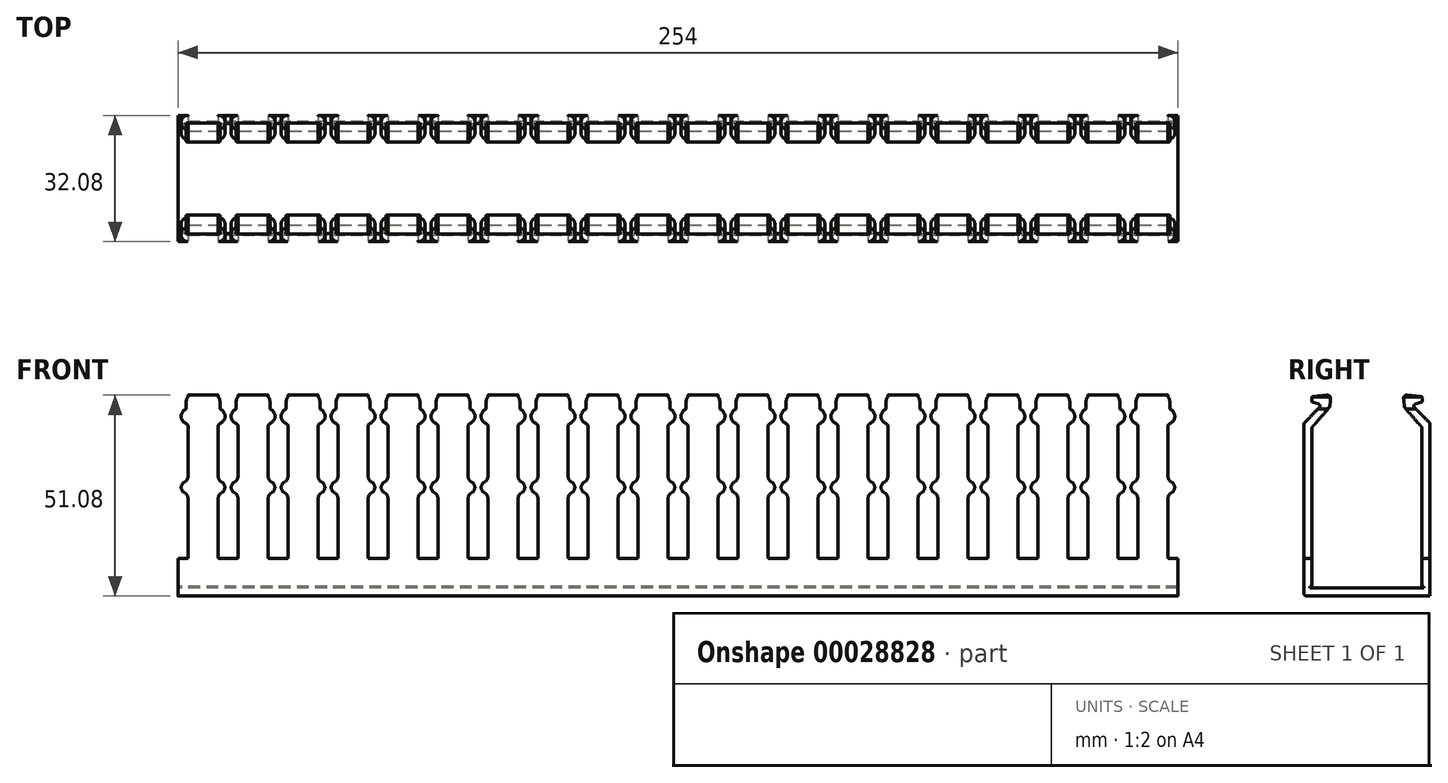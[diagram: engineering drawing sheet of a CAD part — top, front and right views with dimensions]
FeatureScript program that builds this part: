
annotation { "Feature Type Name" : "Feature", "Feature Type Description" : "" }
export const myFeature = defineFeature(function(context is Context, id is Id, definition is map)
    precondition{}
    {
        {
            var Q0;
            Q0=qCreatedBy(makeId("Right.planeOp"),FACE);
            var sketch = newSketch(context, id + "F0", { "sketchPlane" : qUnion([Q0])});
            skLineSegment(sketch, "E0", {"start": v(-14.48, -23.5) * mm, "end": v(-14.48, -23.08) * mm});
            skLineSegment(sketch, "E1", {"start": v(-14.48, -23.08) * mm, "end": v(-14, -23.12) * mm});
            skLineSegment(sketch, "E2", {"start": v(-14, -23.12) * mm, "end": v(-14, 17.02) * mm});
            skArc(sketch, "E3", {"start": v(-14, 17.02) * mm, "mid": v(-13.95, 17.28) * mm, "end": v(-13.81, 17.52) * mm});
            skLineSegment(sketch, "E4", {"start": v(-13.81, 17.52) * mm, "end": v(-9.62, 22.36) * mm});
            skArc(sketch, "E5", {"start": v(-9.62, 22.36) * mm, "mid": v(-9.5, 22.56) * mm, "end": v(-9.44, 22.8) * mm});
            skLineSegment(sketch, "E6", {"start": v(-9.44, 22.8) * mm, "end": v(-9.3, 24.72) * mm});
            skArc(sketch, "E7", {"start": v(-9.3, 24.72) * mm, "mid": v(-9.53, 25.33) * mm, "end": v(-10.13, 25.54) * mm});
            skLineSegment(sketch, "E8", {"start": v(-10.13, 25.54) * mm, "end": v(-13.77, 25.17) * mm});
            skArc(sketch, "E9", {"start": v(-13.77, 25.17) * mm, "mid": v(-13.92, 25.1) * mm, "end": v(-14, 24.94) * mm});
            skLineSegment(sketch, "E10", {"start": v(-14, 24.94) * mm, "end": v(-14.06, 24.06) * mm});
            skArc(sketch, "E11", {"start": v(-14.06, 24.06) * mm, "mid": v(-14.02, 23.9) * mm, "end": v(-13.89, 23.8) * mm});
            skLineSegment(sketch, "E12", {"start": v(-13.89, 23.8) * mm, "end": v(-12.26, 23.23) * mm});
            skArc(sketch, "E13", {"start": v(-12.26, 23.23) * mm, "mid": v(-11.94, 22.87) * mm, "end": v(-12.07, 22.4) * mm});
            skLineSegment(sketch, "E14", {"start": v(-12.07, 22.4) * mm, "end": v(-15.82, 18.57) * mm});
            skArc(sketch, "E15", {"start": v(-15.82, 18.57) * mm, "mid": v(-15.98, 18.32) * mm, "end": v(-16.04, 18.03) * mm});
            skLineSegment(sketch, "E16", {"start": v(-16.04, 18.03) * mm, "end": v(-16.03, -24.78) * mm});
            skArc(sketch, "E17", {"start": v(-16.03, -24.78) * mm, "mid": v(-15.8, -25.32) * mm, "end": v(-15.26, -25.54) * mm});
            skLineSegment(sketch, "E18", {"start": v(-15.26, -25.54) * mm, "end": v(16.03, -25.54) * mm});
            skLineSegment(sketch, "E19", {"start": v(16.03, -25.54) * mm, "end": v(16.04, 18.03) * mm});
            skArc(sketch, "E20", {"start": v(16.04, 18.03) * mm, "mid": v(15.98, 18.32) * mm, "end": v(15.82, 18.57) * mm});
            skLineSegment(sketch, "E21", {"start": v(15.82, 18.57) * mm, "end": v(12.07, 22.4) * mm});
            skArc(sketch, "E22", {"start": v(12.07, 22.4) * mm, "mid": v(11.94, 22.87) * mm, "end": v(12.26, 23.23) * mm});
            skLineSegment(sketch, "E23", {"start": v(12.26, 23.23) * mm, "end": v(13.89, 23.8) * mm});
            skArc(sketch, "E24", {"start": v(13.89, 23.8) * mm, "mid": v(14.02, 23.9) * mm, "end": v(14.06, 24.06) * mm});
            skLineSegment(sketch, "E25", {"start": v(14.06, 24.06) * mm, "end": v(14, 24.94) * mm});
            skArc(sketch, "E26", {"start": v(14, 24.94) * mm, "mid": v(13.92, 25.1) * mm, "end": v(13.77, 25.17) * mm});
            skLineSegment(sketch, "E27", {"start": v(13.77, 25.17) * mm, "end": v(10.13, 25.54) * mm});
            skArc(sketch, "E28", {"start": v(10.13, 25.54) * mm, "mid": v(9.53, 25.33) * mm, "end": v(9.3, 24.72) * mm});
            skLineSegment(sketch, "E29", {"start": v(9.3, 24.72) * mm, "end": v(9.44, 22.8) * mm});
            skArc(sketch, "E30", {"start": v(9.44, 22.8) * mm, "mid": v(9.5, 22.56) * mm, "end": v(9.62, 22.36) * mm});
            skLineSegment(sketch, "E31", {"start": v(9.62, 22.36) * mm, "end": v(13.81, 17.52) * mm});
            skArc(sketch, "E32", {"start": v(13.81, 17.52) * mm, "mid": v(13.95, 17.28) * mm, "end": v(14, 17.02) * mm});
            skLineSegment(sketch, "E33", {"start": v(14, 17.02) * mm, "end": v(14, -23.12) * mm});
            skLineSegment(sketch, "E34", {"start": v(14, -23.12) * mm, "end": v(14.48, -23.08) * mm});
            skLineSegment(sketch, "E35", {"start": v(14.48, -23.08) * mm, "end": v(14.48, -23.5) * mm});
            skLineSegment(sketch, "E36", {"start": v(14.48, -23.5) * mm, "end": v(-14.48, -23.5) * mm});
            skSolve(sketch);
        }
        {
            var Q0;
            Q0=qSketchRegion(id+"F0",true);
            extrude(context, id + "F1", {"entities" : qUnion([Q0]), "endBound" : BoundingType.SYMMETRIC, "depth" : 254 * mm});
        }
        {
            var Q0;
            Q0=qCreatedBy(makeId("Front.planeOp"),FACE);
            var sketch = newSketch(context, id + "F2", { "sketchPlane" : qUnion([Q0])});
            skLineSegment(sketch, "E37.bottom", {"start": v(-2.49, 26.05) * mm, "end": v(2.49, 26.05) * mm});
            skLineSegment(sketch, "E37.top", {"start": v(-2.24, -16.02) * mm, "end": v(2.24, -16.02) * mm});
            skLineSegment(sketch, "E37.right", {"start": v(2.49, 26.05) * mm, "end": v(2.49, 25.07) * mm});
            skPoint(sketch, "E38.visualSharp", {"position": v(2.49, -16.02) * mm});
            skArc(sketch, "E38.filletArc", {"start": v(2.24, -16.02) * mm, "mid": v(2.41, -15.94) * mm, "end": v(2.49, -15.76) * mm});
            skPoint(sketch, "E39.visualSharp", {"position": v(-2.49, -16.02) * mm});
            skArc(sketch, "E39.filletArc", {"start": v(-2.49, -15.76) * mm, "mid": v(-2.41, -15.94) * mm, "end": v(-2.24, -16.02) * mm});
            skArc(sketch, "E40", {"start": v(1.65, 3.46) * mm, "mid": v(0.8, 2.1) * mm, "end": v(1.65, 0.73) * mm});
            skArc(sketch, "E41", {"start": v(1.65, 3.46) * mm, "mid": v(2.26, 4.02) * mm, "end": v(2.49, 4.82) * mm});
            skLineSegment(sketch, "E42", {"start": v(2.33, 2.1) * mm, "end": v(-0.6, 2.1) * mm, "construction": true});
            skArc(sketch, "E43.MirrorC", {"start": v(1.65, 0.73) * mm, "mid": v(2.26, 0.17) * mm, "end": v(2.49, -0.63) * mm});
            skLineSegment(sketch, "E44.trimOffspring", {"start": v(2.49, -0.63) * mm, "end": v(2.49, -15.76) * mm});
            skArc(sketch, "E45.MirrorCS", {"start": v(-1.65, 3.46) * mm, "mid": v(-0.8, 2.1) * mm, "end": v(-1.65, 0.73) * mm});
            skArc(sketch, "E46.MirrorCS", {"start": v(-1.65, 3.46) * mm, "mid": v(-2.26, 4.02) * mm, "end": v(-2.49, 4.82) * mm});
            skArc(sketch, "E47.MirrorCS", {"start": v(-1.65, 0.73) * mm, "mid": v(-2.26, 0.17) * mm, "end": v(-2.49, -0.63) * mm});
            skLineSegment(sketch, "E48.trimOffspring", {"start": v(-2.49, -0.63) * mm, "end": v(-2.49, -15.76) * mm});
            skArc(sketch, "E49", {"start": v(2.08, 22) * mm, "mid": v(0.78, 20.17) * mm, "end": v(2.06, 18.33) * mm});
            skLineSegment(sketch, "E50.trimOffspring", {"start": v(2.49, 17.71) * mm, "end": v(2.49, 4.82) * mm});
            skPoint(sketch, "E51.visualSharp", {"position": v(2.49, 18.23) * mm});
            skArc(sketch, "E51.filletArc", {"start": v(2.49, 17.71) * mm, "mid": v(2.37, 18.09) * mm, "end": v(2.06, 18.33) * mm});
            skLineSegment(sketch, "E52", {"start": v(2.08, 22) * mm, "end": v(2.1, 24.06) * mm});
            skPoint(sketch, "E53.orphan", {"position": v(2.08, 22) * mm});
            skArc(sketch, "E54", {"start": v(2.49, 25.07) * mm, "mid": v(2.2, 24.6) * mm, "end": v(2.1, 24.06) * mm});
            skArc(sketch, "E55.MirrorCS", {"start": v(-2.49, 17.71) * mm, "mid": v(-2.37, 18.09) * mm, "end": v(-2.06, 18.33) * mm});
            skArc(sketch, "E56.MirrorCS", {"start": v(-2.08, 22) * mm, "mid": v(-0.78, 20.17) * mm, "end": v(-2.06, 18.33) * mm});
            skPoint(sketch, "E57.MirrorP", {"position": v(-2.08, 22) * mm});
            skLineSegment(sketch, "E58.MirrorCS", {"start": v(-2.08, 22) * mm, "end": v(-2.1, 24.06) * mm});
            skLineSegment(sketch, "E59.MirrorCS", {"start": v(-2.49, 17.71) * mm, "end": v(-2.49, 4.82) * mm});
            skLineSegment(sketch, "E60.MirrorCS", {"start": v(-2.49, 26.05) * mm, "end": v(-2.49, 25.07) * mm});
            skArc(sketch, "E61.MirrorCS", {"start": v(-2.49, 25.07) * mm, "mid": v(-2.2, 24.6) * mm, "end": v(-2.1, 24.06) * mm});
            skPoint(sketch, "E62.MirrorP", {"position": v(-2.49, 18.23) * mm});
            skPoint(sketch, "E63.1.0.1", {"position": v(14.78, 22) * mm});
            skArc(sketch, "E63.1.0.6", {"start": v(10.21, 25.07) * mm, "mid": v(10.5, 24.6) * mm, "end": v(10.6, 24.06) * mm});
            skLineSegment(sketch, "E63.1.0.7", {"start": v(10.21, 26.05) * mm, "end": v(10.21, 25.07) * mm});
            skLineSegment(sketch, "E63.1.0.9", {"start": v(10.62, 22) * mm, "end": v(10.6, 24.06) * mm});
            skArc(sketch, "E63.1.0.11", {"start": v(15.19, 25.07) * mm, "mid": v(14.9, 24.6) * mm, "end": v(14.8, 24.06) * mm});
            skLineSegment(sketch, "E63.1.0.12", {"start": v(14.78, 22) * mm, "end": v(14.8, 24.06) * mm});
            skLineSegment(sketch, "E63.1.0.21", {"start": v(10.21, 26.05) * mm, "end": v(15.19, 26.05) * mm});
            skLineSegment(sketch, "E63.1.0.22", {"start": v(15.19, 26.05) * mm, "end": v(15.19, 25.07) * mm});
            skArc(sketch, "E63.1.0.26", {"start": v(14.78, 22) * mm, "mid": v(13.48, 20.17) * mm, "end": v(14.76, 18.33) * mm});
            skPoint(sketch, "E63.1.0.27", {"position": v(10.21, 18.23) * mm});
            skPoint(sketch, "E63.1.0.31", {"position": v(15.19, 18.23) * mm});
            skPoint(sketch, "E63.1.0.33", {"position": v(10.62, 22) * mm});
            skArc(sketch, "E63.1.0.34", {"start": v(10.62, 22) * mm, "mid": v(11.92, 20.17) * mm, "end": v(10.64, 18.33) * mm});
            skArc(sketch, "E63.1.0.43", {"start": v(15.19, 17.71) * mm, "mid": v(15.07, 18.09) * mm, "end": v(14.76, 18.33) * mm});
            skArc(sketch, "E63.1.0.44", {"start": v(10.21, 17.71) * mm, "mid": v(10.33, 18.09) * mm, "end": v(10.64, 18.33) * mm});
            skArc(sketch, "E63.1.0.48", {"start": v(14.35, 3.46) * mm, "mid": v(13.5, 2.1) * mm, "end": v(14.35, 0.73) * mm});
            skLineSegment(sketch, "E63.1.0.52", {"start": v(15.03, 2.1) * mm, "end": v(12.1, 2.1) * mm, "construction": true});
            skArc(sketch, "E63.1.0.59", {"start": v(11.05, 3.46) * mm, "mid": v(11.9, 2.1) * mm, "end": v(11.05, 0.73) * mm});
            skLineSegment(sketch, "E63.1.0.61", {"start": v(10.21, 17.71) * mm, "end": v(10.21, 4.82) * mm});
            skArc(sketch, "E63.1.0.73", {"start": v(14.35, 0.73) * mm, "mid": v(14.96, 0.17) * mm, "end": v(15.19, -0.63) * mm});
            skArc(sketch, "E63.1.0.74", {"start": v(14.35, 3.46) * mm, "mid": v(14.96, 4.02) * mm, "end": v(15.19, 4.82) * mm});
            skArc(sketch, "E63.1.0.75", {"start": v(11.05, 0.73) * mm, "mid": v(10.44, 0.17) * mm, "end": v(10.21, -0.63) * mm});
            skArc(sketch, "E63.1.0.76", {"start": v(11.05, 3.46) * mm, "mid": v(10.44, 4.02) * mm, "end": v(10.21, 4.82) * mm});
            skLineSegment(sketch, "E63.1.0.77", {"start": v(15.19, 17.71) * mm, "end": v(15.19, 4.82) * mm});
            skLineSegment(sketch, "E63.1.0.78", {"start": v(15.19, -0.63) * mm, "end": v(15.19, -15.76) * mm});
            skLineSegment(sketch, "E63.1.0.79", {"start": v(10.21, -0.63) * mm, "end": v(10.21, -15.76) * mm});
            skLineSegment(sketch, "E63.1.0.80", {"start": v(10.46, -16.02) * mm, "end": v(14.94, -16.02) * mm});
            skPoint(sketch, "E63.1.0.81", {"position": v(10.21, -16.02) * mm});
            skPoint(sketch, "E63.1.0.82", {"position": v(15.19, -16.02) * mm});
            skArc(sketch, "E63.1.0.93", {"start": v(14.94, -16.02) * mm, "mid": v(15.11, -15.94) * mm, "end": v(15.19, -15.76) * mm});
            skArc(sketch, "E63.1.0.94", {"start": v(10.21, -15.76) * mm, "mid": v(10.29, -15.94) * mm, "end": v(10.46, -16.02) * mm});
            skPoint(sketch, "E63.2.0.1", {"position": v(27.48, 22) * mm});
            skArc(sketch, "E63.2.0.6", {"start": v(22.91, 25.07) * mm, "mid": v(23.2, 24.6) * mm, "end": v(23.3, 24.06) * mm});
            skLineSegment(sketch, "E63.2.0.7", {"start": v(22.91, 26.05) * mm, "end": v(22.91, 25.07) * mm});
            skLineSegment(sketch, "E63.2.0.9", {"start": v(23.32, 22) * mm, "end": v(23.3, 24.06) * mm});
            skArc(sketch, "E63.2.0.11", {"start": v(27.89, 25.07) * mm, "mid": v(27.6, 24.6) * mm, "end": v(27.5, 24.06) * mm});
            skLineSegment(sketch, "E63.2.0.12", {"start": v(27.48, 22) * mm, "end": v(27.5, 24.06) * mm});
            skLineSegment(sketch, "E63.2.0.21", {"start": v(22.91, 26.05) * mm, "end": v(27.89, 26.05) * mm});
            skLineSegment(sketch, "E63.2.0.22", {"start": v(27.89, 26.05) * mm, "end": v(27.89, 25.07) * mm});
            skArc(sketch, "E63.2.0.26", {"start": v(27.48, 22) * mm, "mid": v(26.18, 20.17) * mm, "end": v(27.46, 18.33) * mm});
            skPoint(sketch, "E63.2.0.27", {"position": v(22.91, 18.23) * mm});
            skPoint(sketch, "E63.2.0.31", {"position": v(27.89, 18.23) * mm});
            skPoint(sketch, "E63.2.0.33", {"position": v(23.32, 22) * mm});
            skArc(sketch, "E63.2.0.34", {"start": v(23.32, 22) * mm, "mid": v(24.62, 20.17) * mm, "end": v(23.34, 18.33) * mm});
            skArc(sketch, "E63.2.0.43", {"start": v(27.89, 17.71) * mm, "mid": v(27.77, 18.09) * mm, "end": v(27.46, 18.33) * mm});
            skArc(sketch, "E63.2.0.44", {"start": v(22.91, 17.71) * mm, "mid": v(23.03, 18.09) * mm, "end": v(23.34, 18.33) * mm});
            skArc(sketch, "E63.2.0.48", {"start": v(27.05, 3.46) * mm, "mid": v(26.2, 2.1) * mm, "end": v(27.05, 0.73) * mm});
            skLineSegment(sketch, "E63.2.0.52", {"start": v(27.73, 2.1) * mm, "end": v(24.8, 2.1) * mm, "construction": true});
            skArc(sketch, "E63.2.0.59", {"start": v(23.75, 3.46) * mm, "mid": v(24.6, 2.1) * mm, "end": v(23.75, 0.73) * mm});
            skLineSegment(sketch, "E63.2.0.61", {"start": v(22.91, 17.71) * mm, "end": v(22.91, 4.82) * mm});
            skArc(sketch, "E63.2.0.73", {"start": v(27.05, 0.73) * mm, "mid": v(27.66, 0.17) * mm, "end": v(27.89, -0.63) * mm});
            skArc(sketch, "E63.2.0.74", {"start": v(27.05, 3.46) * mm, "mid": v(27.66, 4.02) * mm, "end": v(27.89, 4.82) * mm});
            skArc(sketch, "E63.2.0.75", {"start": v(23.75, 0.73) * mm, "mid": v(23.14, 0.17) * mm, "end": v(22.91, -0.63) * mm});
            skArc(sketch, "E63.2.0.76", {"start": v(23.75, 3.46) * mm, "mid": v(23.14, 4.02) * mm, "end": v(22.91, 4.82) * mm});
            skLineSegment(sketch, "E63.2.0.77", {"start": v(27.89, 17.71) * mm, "end": v(27.89, 4.82) * mm});
            skLineSegment(sketch, "E63.2.0.78", {"start": v(27.89, -0.63) * mm, "end": v(27.89, -15.76) * mm});
            skLineSegment(sketch, "E63.2.0.79", {"start": v(22.91, -0.63) * mm, "end": v(22.91, -15.76) * mm});
            skLineSegment(sketch, "E63.2.0.80", {"start": v(23.16, -16.02) * mm, "end": v(27.64, -16.02) * mm});
            skPoint(sketch, "E63.2.0.81", {"position": v(22.91, -16.02) * mm});
            skPoint(sketch, "E63.2.0.82", {"position": v(27.89, -16.02) * mm});
            skArc(sketch, "E63.2.0.93", {"start": v(27.64, -16.02) * mm, "mid": v(27.81, -15.94) * mm, "end": v(27.89, -15.76) * mm});
            skArc(sketch, "E63.2.0.94", {"start": v(22.91, -15.76) * mm, "mid": v(22.99, -15.94) * mm, "end": v(23.16, -16.02) * mm});
            skPoint(sketch, "E63.3.0.1", {"position": v(40.18, 22) * mm});
            skArc(sketch, "E63.3.0.6", {"start": v(35.61, 25.07) * mm, "mid": v(35.9, 24.6) * mm, "end": v(36, 24.06) * mm});
            skLineSegment(sketch, "E63.3.0.7", {"start": v(35.61, 26.05) * mm, "end": v(35.61, 25.07) * mm});
            skLineSegment(sketch, "E63.3.0.9", {"start": v(36.02, 22) * mm, "end": v(36, 24.06) * mm});
            skArc(sketch, "E63.3.0.11", {"start": v(40.59, 25.07) * mm, "mid": v(40.3, 24.6) * mm, "end": v(40.2, 24.06) * mm});
            skLineSegment(sketch, "E63.3.0.12", {"start": v(40.18, 22) * mm, "end": v(40.2, 24.06) * mm});
            skLineSegment(sketch, "E63.3.0.21", {"start": v(35.61, 26.05) * mm, "end": v(40.59, 26.05) * mm});
            skLineSegment(sketch, "E63.3.0.22", {"start": v(40.59, 26.05) * mm, "end": v(40.59, 25.07) * mm});
            skArc(sketch, "E63.3.0.26", {"start": v(40.18, 22) * mm, "mid": v(38.88, 20.17) * mm, "end": v(40.16, 18.33) * mm});
            skPoint(sketch, "E63.3.0.27", {"position": v(35.61, 18.23) * mm});
            skPoint(sketch, "E63.3.0.31", {"position": v(40.59, 18.23) * mm});
            skPoint(sketch, "E63.3.0.33", {"position": v(36.02, 22) * mm});
            skArc(sketch, "E63.3.0.34", {"start": v(36.02, 22) * mm, "mid": v(37.32, 20.17) * mm, "end": v(36.04, 18.33) * mm});
            skArc(sketch, "E63.3.0.43", {"start": v(40.59, 17.71) * mm, "mid": v(40.47, 18.09) * mm, "end": v(40.16, 18.33) * mm});
            skArc(sketch, "E63.3.0.44", {"start": v(35.61, 17.71) * mm, "mid": v(35.73, 18.09) * mm, "end": v(36.04, 18.33) * mm});
            skArc(sketch, "E63.3.0.48", {"start": v(39.75, 3.46) * mm, "mid": v(38.9, 2.1) * mm, "end": v(39.75, 0.73) * mm});
            skLineSegment(sketch, "E63.3.0.52", {"start": v(40.43, 2.1) * mm, "end": v(37.5, 2.1) * mm, "construction": true});
            skArc(sketch, "E63.3.0.59", {"start": v(36.45, 3.46) * mm, "mid": v(37.3, 2.1) * mm, "end": v(36.45, 0.73) * mm});
            skLineSegment(sketch, "E63.3.0.61", {"start": v(35.61, 17.71) * mm, "end": v(35.61, 4.82) * mm});
            skArc(sketch, "E63.3.0.73", {"start": v(39.75, 0.73) * mm, "mid": v(40.36, 0.17) * mm, "end": v(40.59, -0.63) * mm});
            skArc(sketch, "E63.3.0.74", {"start": v(39.75, 3.46) * mm, "mid": v(40.36, 4.02) * mm, "end": v(40.59, 4.82) * mm});
            skArc(sketch, "E63.3.0.75", {"start": v(36.45, 0.73) * mm, "mid": v(35.84, 0.17) * mm, "end": v(35.61, -0.63) * mm});
            skArc(sketch, "E63.3.0.76", {"start": v(36.45, 3.46) * mm, "mid": v(35.84, 4.02) * mm, "end": v(35.61, 4.82) * mm});
            skLineSegment(sketch, "E63.3.0.77", {"start": v(40.59, 17.71) * mm, "end": v(40.59, 4.82) * mm});
            skLineSegment(sketch, "E63.3.0.78", {"start": v(40.59, -0.63) * mm, "end": v(40.59, -15.76) * mm});
            skLineSegment(sketch, "E63.3.0.79", {"start": v(35.61, -0.63) * mm, "end": v(35.61, -15.76) * mm});
            skLineSegment(sketch, "E63.3.0.80", {"start": v(35.86, -16.02) * mm, "end": v(40.34, -16.02) * mm});
            skPoint(sketch, "E63.3.0.81", {"position": v(35.61, -16.02) * mm});
            skPoint(sketch, "E63.3.0.82", {"position": v(40.59, -16.02) * mm});
            skArc(sketch, "E63.3.0.93", {"start": v(40.34, -16.02) * mm, "mid": v(40.51, -15.94) * mm, "end": v(40.59, -15.76) * mm});
            skArc(sketch, "E63.3.0.94", {"start": v(35.61, -15.76) * mm, "mid": v(35.69, -15.94) * mm, "end": v(35.86, -16.02) * mm});
            skPoint(sketch, "E63.4.0.1", {"position": v(52.88, 22) * mm});
            skArc(sketch, "E63.4.0.6", {"start": v(48.31, 25.07) * mm, "mid": v(48.6, 24.6) * mm, "end": v(48.7, 24.06) * mm});
            skLineSegment(sketch, "E63.4.0.7", {"start": v(48.31, 26.05) * mm, "end": v(48.31, 25.07) * mm});
            skLineSegment(sketch, "E63.4.0.9", {"start": v(48.72, 22) * mm, "end": v(48.7, 24.06) * mm});
            skArc(sketch, "E63.4.0.11", {"start": v(53.29, 25.07) * mm, "mid": v(53, 24.6) * mm, "end": v(52.9, 24.06) * mm});
            skLineSegment(sketch, "E63.4.0.12", {"start": v(52.88, 22) * mm, "end": v(52.9, 24.06) * mm});
            skLineSegment(sketch, "E63.4.0.21", {"start": v(48.31, 26.05) * mm, "end": v(53.29, 26.05) * mm});
            skLineSegment(sketch, "E63.4.0.22", {"start": v(53.29, 26.05) * mm, "end": v(53.29, 25.07) * mm});
            skArc(sketch, "E63.4.0.26", {"start": v(52.88, 22) * mm, "mid": v(51.58, 20.17) * mm, "end": v(52.86, 18.33) * mm});
            skPoint(sketch, "E63.4.0.27", {"position": v(48.31, 18.23) * mm});
            skPoint(sketch, "E63.4.0.31", {"position": v(53.29, 18.23) * mm});
            skPoint(sketch, "E63.4.0.33", {"position": v(48.72, 22) * mm});
            skArc(sketch, "E63.4.0.34", {"start": v(48.72, 22) * mm, "mid": v(50.02, 20.17) * mm, "end": v(48.74, 18.33) * mm});
            skArc(sketch, "E63.4.0.43", {"start": v(53.29, 17.71) * mm, "mid": v(53.17, 18.09) * mm, "end": v(52.86, 18.33) * mm});
            skArc(sketch, "E63.4.0.44", {"start": v(48.31, 17.71) * mm, "mid": v(48.43, 18.09) * mm, "end": v(48.74, 18.33) * mm});
            skArc(sketch, "E63.4.0.48", {"start": v(52.45, 3.46) * mm, "mid": v(51.6, 2.1) * mm, "end": v(52.45, 0.73) * mm});
            skLineSegment(sketch, "E63.4.0.52", {"start": v(53.13, 2.1) * mm, "end": v(50.2, 2.1) * mm, "construction": true});
            skArc(sketch, "E63.4.0.59", {"start": v(49.15, 3.46) * mm, "mid": v(50, 2.1) * mm, "end": v(49.15, 0.73) * mm});
            skLineSegment(sketch, "E63.4.0.61", {"start": v(48.31, 17.71) * mm, "end": v(48.31, 4.82) * mm});
            skArc(sketch, "E63.4.0.73", {"start": v(52.45, 0.73) * mm, "mid": v(53.06, 0.17) * mm, "end": v(53.29, -0.63) * mm});
            skArc(sketch, "E63.4.0.74", {"start": v(52.45, 3.46) * mm, "mid": v(53.06, 4.02) * mm, "end": v(53.29, 4.82) * mm});
            skArc(sketch, "E63.4.0.75", {"start": v(49.15, 0.73) * mm, "mid": v(48.54, 0.17) * mm, "end": v(48.31, -0.63) * mm});
            skArc(sketch, "E63.4.0.76", {"start": v(49.15, 3.46) * mm, "mid": v(48.54, 4.02) * mm, "end": v(48.31, 4.82) * mm});
            skLineSegment(sketch, "E63.4.0.77", {"start": v(53.29, 17.71) * mm, "end": v(53.29, 4.82) * mm});
            skLineSegment(sketch, "E63.4.0.78", {"start": v(53.29, -0.63) * mm, "end": v(53.29, -15.76) * mm});
            skLineSegment(sketch, "E63.4.0.79", {"start": v(48.31, -0.63) * mm, "end": v(48.31, -15.76) * mm});
            skLineSegment(sketch, "E63.4.0.80", {"start": v(48.56, -16.02) * mm, "end": v(53.04, -16.02) * mm});
            skPoint(sketch, "E63.4.0.81", {"position": v(48.31, -16.02) * mm});
            skPoint(sketch, "E63.4.0.82", {"position": v(53.29, -16.02) * mm});
            skArc(sketch, "E63.4.0.93", {"start": v(53.04, -16.02) * mm, "mid": v(53.21, -15.94) * mm, "end": v(53.29, -15.76) * mm});
            skArc(sketch, "E63.4.0.94", {"start": v(48.31, -15.76) * mm, "mid": v(48.39, -15.94) * mm, "end": v(48.56, -16.02) * mm});
            skPoint(sketch, "E63.5.0.1", {"position": v(65.58, 22) * mm});
            skArc(sketch, "E63.5.0.6", {"start": v(61.01, 25.07) * mm, "mid": v(61.3, 24.6) * mm, "end": v(61.4, 24.06) * mm});
            skLineSegment(sketch, "E63.5.0.7", {"start": v(61.01, 26.05) * mm, "end": v(61.01, 25.07) * mm});
            skLineSegment(sketch, "E63.5.0.9", {"start": v(61.42, 22) * mm, "end": v(61.4, 24.06) * mm});
            skArc(sketch, "E63.5.0.11", {"start": v(65.99, 25.07) * mm, "mid": v(65.7, 24.6) * mm, "end": v(65.6, 24.06) * mm});
            skLineSegment(sketch, "E63.5.0.12", {"start": v(65.58, 22) * mm, "end": v(65.6, 24.06) * mm});
            skLineSegment(sketch, "E63.5.0.21", {"start": v(61.01, 26.05) * mm, "end": v(65.99, 26.05) * mm});
            skLineSegment(sketch, "E63.5.0.22", {"start": v(65.99, 26.05) * mm, "end": v(65.99, 25.07) * mm});
            skArc(sketch, "E63.5.0.26", {"start": v(65.58, 22) * mm, "mid": v(64.28, 20.17) * mm, "end": v(65.56, 18.33) * mm});
            skPoint(sketch, "E63.5.0.27", {"position": v(61.01, 18.23) * mm});
            skPoint(sketch, "E63.5.0.31", {"position": v(65.99, 18.23) * mm});
            skPoint(sketch, "E63.5.0.33", {"position": v(61.42, 22) * mm});
            skArc(sketch, "E63.5.0.34", {"start": v(61.42, 22) * mm, "mid": v(62.72, 20.17) * mm, "end": v(61.44, 18.33) * mm});
            skArc(sketch, "E63.5.0.43", {"start": v(65.99, 17.71) * mm, "mid": v(65.87, 18.09) * mm, "end": v(65.56, 18.33) * mm});
            skArc(sketch, "E63.5.0.44", {"start": v(61.01, 17.71) * mm, "mid": v(61.13, 18.09) * mm, "end": v(61.44, 18.33) * mm});
            skArc(sketch, "E63.5.0.48", {"start": v(65.15, 3.46) * mm, "mid": v(64.3, 2.1) * mm, "end": v(65.15, 0.73) * mm});
            skLineSegment(sketch, "E63.5.0.52", {"start": v(65.83, 2.1) * mm, "end": v(62.9, 2.1) * mm, "construction": true});
            skArc(sketch, "E63.5.0.59", {"start": v(61.85, 3.46) * mm, "mid": v(62.7, 2.1) * mm, "end": v(61.85, 0.73) * mm});
            skLineSegment(sketch, "E63.5.0.61", {"start": v(61.01, 17.71) * mm, "end": v(61.01, 4.82) * mm});
            skArc(sketch, "E63.5.0.73", {"start": v(65.15, 0.73) * mm, "mid": v(65.76, 0.17) * mm, "end": v(65.99, -0.63) * mm});
            skArc(sketch, "E63.5.0.74", {"start": v(65.15, 3.46) * mm, "mid": v(65.76, 4.02) * mm, "end": v(65.99, 4.82) * mm});
            skArc(sketch, "E63.5.0.75", {"start": v(61.85, 0.73) * mm, "mid": v(61.24, 0.17) * mm, "end": v(61.01, -0.63) * mm});
            skArc(sketch, "E63.5.0.76", {"start": v(61.85, 3.46) * mm, "mid": v(61.24, 4.02) * mm, "end": v(61.01, 4.82) * mm});
            skLineSegment(sketch, "E63.5.0.77", {"start": v(65.99, 17.71) * mm, "end": v(65.99, 4.82) * mm});
            skLineSegment(sketch, "E63.5.0.78", {"start": v(65.99, -0.63) * mm, "end": v(65.99, -15.76) * mm});
            skLineSegment(sketch, "E63.5.0.79", {"start": v(61.01, -0.63) * mm, "end": v(61.01, -15.76) * mm});
            skLineSegment(sketch, "E63.5.0.80", {"start": v(61.26, -16.02) * mm, "end": v(65.74, -16.02) * mm});
            skPoint(sketch, "E63.5.0.81", {"position": v(61.01, -16.02) * mm});
            skPoint(sketch, "E63.5.0.82", {"position": v(65.99, -16.02) * mm});
            skArc(sketch, "E63.5.0.93", {"start": v(65.74, -16.02) * mm, "mid": v(65.91, -15.94) * mm, "end": v(65.99, -15.76) * mm});
            skArc(sketch, "E63.5.0.94", {"start": v(61.01, -15.76) * mm, "mid": v(61.09, -15.94) * mm, "end": v(61.26, -16.02) * mm});
            skPoint(sketch, "E63.6.0.1", {"position": v(78.28, 22) * mm});
            skArc(sketch, "E63.6.0.6", {"start": v(73.71, 25.07) * mm, "mid": v(74, 24.6) * mm, "end": v(74.1, 24.06) * mm});
            skLineSegment(sketch, "E63.6.0.7", {"start": v(73.71, 26.05) * mm, "end": v(73.71, 25.07) * mm});
            skLineSegment(sketch, "E63.6.0.9", {"start": v(74.12, 22) * mm, "end": v(74.1, 24.06) * mm});
            skArc(sketch, "E63.6.0.11", {"start": v(78.69, 25.07) * mm, "mid": v(78.4, 24.6) * mm, "end": v(78.3, 24.06) * mm});
            skLineSegment(sketch, "E63.6.0.12", {"start": v(78.28, 22) * mm, "end": v(78.3, 24.06) * mm});
            skLineSegment(sketch, "E63.6.0.21", {"start": v(73.71, 26.05) * mm, "end": v(78.69, 26.05) * mm});
            skLineSegment(sketch, "E63.6.0.22", {"start": v(78.69, 26.05) * mm, "end": v(78.69, 25.07) * mm});
            skArc(sketch, "E63.6.0.26", {"start": v(78.28, 22) * mm, "mid": v(76.98, 20.17) * mm, "end": v(78.26, 18.33) * mm});
            skPoint(sketch, "E63.6.0.27", {"position": v(73.71, 18.23) * mm});
            skPoint(sketch, "E63.6.0.31", {"position": v(78.69, 18.23) * mm});
            skPoint(sketch, "E63.6.0.33", {"position": v(74.12, 22) * mm});
            skArc(sketch, "E63.6.0.34", {"start": v(74.12, 22) * mm, "mid": v(75.42, 20.17) * mm, "end": v(74.14, 18.33) * mm});
            skArc(sketch, "E63.6.0.43", {"start": v(78.69, 17.71) * mm, "mid": v(78.57, 18.09) * mm, "end": v(78.26, 18.33) * mm});
            skArc(sketch, "E63.6.0.44", {"start": v(73.71, 17.71) * mm, "mid": v(73.83, 18.09) * mm, "end": v(74.14, 18.33) * mm});
            skArc(sketch, "E63.6.0.48", {"start": v(77.85, 3.46) * mm, "mid": v(77, 2.1) * mm, "end": v(77.85, 0.73) * mm});
            skLineSegment(sketch, "E63.6.0.52", {"start": v(78.53, 2.1) * mm, "end": v(75.6, 2.1) * mm, "construction": true});
            skArc(sketch, "E63.6.0.59", {"start": v(74.55, 3.46) * mm, "mid": v(75.4, 2.1) * mm, "end": v(74.55, 0.73) * mm});
            skLineSegment(sketch, "E63.6.0.61", {"start": v(73.71, 17.71) * mm, "end": v(73.71, 4.82) * mm});
            skArc(sketch, "E63.6.0.73", {"start": v(77.85, 0.73) * mm, "mid": v(78.46, 0.17) * mm, "end": v(78.69, -0.63) * mm});
            skArc(sketch, "E63.6.0.74", {"start": v(77.85, 3.46) * mm, "mid": v(78.46, 4.02) * mm, "end": v(78.69, 4.82) * mm});
            skArc(sketch, "E63.6.0.75", {"start": v(74.55, 0.73) * mm, "mid": v(73.94, 0.17) * mm, "end": v(73.71, -0.63) * mm});
            skArc(sketch, "E63.6.0.76", {"start": v(74.55, 3.46) * mm, "mid": v(73.94, 4.02) * mm, "end": v(73.71, 4.82) * mm});
            skLineSegment(sketch, "E63.6.0.77", {"start": v(78.69, 17.71) * mm, "end": v(78.69, 4.82) * mm});
            skLineSegment(sketch, "E63.6.0.78", {"start": v(78.69, -0.63) * mm, "end": v(78.69, -15.76) * mm});
            skLineSegment(sketch, "E63.6.0.79", {"start": v(73.71, -0.63) * mm, "end": v(73.71, -15.76) * mm});
            skLineSegment(sketch, "E63.6.0.80", {"start": v(73.96, -16.02) * mm, "end": v(78.44, -16.02) * mm});
            skPoint(sketch, "E63.6.0.81", {"position": v(73.71, -16.02) * mm});
            skPoint(sketch, "E63.6.0.82", {"position": v(78.69, -16.02) * mm});
            skArc(sketch, "E63.6.0.93", {"start": v(78.44, -16.02) * mm, "mid": v(78.61, -15.94) * mm, "end": v(78.69, -15.76) * mm});
            skArc(sketch, "E63.6.0.94", {"start": v(73.71, -15.76) * mm, "mid": v(73.79, -15.94) * mm, "end": v(73.96, -16.02) * mm});
            skPoint(sketch, "E63.7.0.1", {"position": v(90.98, 22) * mm});
            skArc(sketch, "E63.7.0.6", {"start": v(86.41, 25.07) * mm, "mid": v(86.7, 24.6) * mm, "end": v(86.8, 24.06) * mm});
            skLineSegment(sketch, "E63.7.0.7", {"start": v(86.41, 26.05) * mm, "end": v(86.41, 25.07) * mm});
            skLineSegment(sketch, "E63.7.0.9", {"start": v(86.82, 22) * mm, "end": v(86.8, 24.06) * mm});
            skArc(sketch, "E63.7.0.11", {"start": v(91.39, 25.07) * mm, "mid": v(91.1, 24.6) * mm, "end": v(91, 24.06) * mm});
            skLineSegment(sketch, "E63.7.0.12", {"start": v(90.98, 22) * mm, "end": v(91, 24.06) * mm});
            skLineSegment(sketch, "E63.7.0.21", {"start": v(86.41, 26.05) * mm, "end": v(91.39, 26.05) * mm});
            skLineSegment(sketch, "E63.7.0.22", {"start": v(91.39, 26.05) * mm, "end": v(91.39, 25.07) * mm});
            skArc(sketch, "E63.7.0.26", {"start": v(90.98, 22) * mm, "mid": v(89.68, 20.17) * mm, "end": v(90.96, 18.33) * mm});
            skPoint(sketch, "E63.7.0.27", {"position": v(86.41, 18.23) * mm});
            skPoint(sketch, "E63.7.0.31", {"position": v(91.39, 18.23) * mm});
            skPoint(sketch, "E63.7.0.33", {"position": v(86.82, 22) * mm});
            skArc(sketch, "E63.7.0.34", {"start": v(86.82, 22) * mm, "mid": v(88.12, 20.17) * mm, "end": v(86.84, 18.33) * mm});
            skArc(sketch, "E63.7.0.43", {"start": v(91.39, 17.71) * mm, "mid": v(91.27, 18.09) * mm, "end": v(90.96, 18.33) * mm});
            skArc(sketch, "E63.7.0.44", {"start": v(86.41, 17.71) * mm, "mid": v(86.53, 18.09) * mm, "end": v(86.84, 18.33) * mm});
            skArc(sketch, "E63.7.0.48", {"start": v(90.55, 3.46) * mm, "mid": v(89.7, 2.1) * mm, "end": v(90.55, 0.73) * mm});
            skLineSegment(sketch, "E63.7.0.52", {"start": v(91.23, 2.1) * mm, "end": v(88.3, 2.1) * mm, "construction": true});
            skArc(sketch, "E63.7.0.59", {"start": v(87.25, 3.46) * mm, "mid": v(88.1, 2.1) * mm, "end": v(87.25, 0.73) * mm});
            skLineSegment(sketch, "E63.7.0.61", {"start": v(86.41, 17.71) * mm, "end": v(86.41, 4.82) * mm});
            skArc(sketch, "E63.7.0.73", {"start": v(90.55, 0.73) * mm, "mid": v(91.16, 0.17) * mm, "end": v(91.39, -0.63) * mm});
            skArc(sketch, "E63.7.0.74", {"start": v(90.55, 3.46) * mm, "mid": v(91.16, 4.02) * mm, "end": v(91.39, 4.82) * mm});
            skArc(sketch, "E63.7.0.75", {"start": v(87.25, 0.73) * mm, "mid": v(86.64, 0.17) * mm, "end": v(86.41, -0.63) * mm});
            skArc(sketch, "E63.7.0.76", {"start": v(87.25, 3.46) * mm, "mid": v(86.64, 4.02) * mm, "end": v(86.41, 4.82) * mm});
            skLineSegment(sketch, "E63.7.0.77", {"start": v(91.39, 17.71) * mm, "end": v(91.39, 4.82) * mm});
            skLineSegment(sketch, "E63.7.0.78", {"start": v(91.39, -0.63) * mm, "end": v(91.39, -15.76) * mm});
            skLineSegment(sketch, "E63.7.0.79", {"start": v(86.41, -0.63) * mm, "end": v(86.41, -15.76) * mm});
            skLineSegment(sketch, "E63.7.0.80", {"start": v(86.66, -16.02) * mm, "end": v(91.14, -16.02) * mm});
            skPoint(sketch, "E63.7.0.81", {"position": v(86.41, -16.02) * mm});
            skPoint(sketch, "E63.7.0.82", {"position": v(91.39, -16.02) * mm});
            skArc(sketch, "E63.7.0.93", {"start": v(91.14, -16.02) * mm, "mid": v(91.31, -15.94) * mm, "end": v(91.39, -15.76) * mm});
            skArc(sketch, "E63.7.0.94", {"start": v(86.41, -15.76) * mm, "mid": v(86.49, -15.94) * mm, "end": v(86.66, -16.02) * mm});
            skPoint(sketch, "E63.8.0.1", {"position": v(103.68, 22) * mm});
            skArc(sketch, "E63.8.0.6", {"start": v(99.11, 25.07) * mm, "mid": v(99.4, 24.6) * mm, "end": v(99.5, 24.06) * mm});
            skLineSegment(sketch, "E63.8.0.7", {"start": v(99.11, 26.05) * mm, "end": v(99.11, 25.07) * mm});
            skLineSegment(sketch, "E63.8.0.9", {"start": v(99.52, 22) * mm, "end": v(99.5, 24.06) * mm});
            skArc(sketch, "E63.8.0.11", {"start": v(104.09, 25.07) * mm, "mid": v(103.8, 24.6) * mm, "end": v(103.7, 24.06) * mm});
            skLineSegment(sketch, "E63.8.0.12", {"start": v(103.68, 22) * mm, "end": v(103.7, 24.06) * mm});
            skLineSegment(sketch, "E63.8.0.21", {"start": v(99.11, 26.05) * mm, "end": v(104.09, 26.05) * mm});
            skLineSegment(sketch, "E63.8.0.22", {"start": v(104.09, 26.05) * mm, "end": v(104.09, 25.07) * mm});
            skArc(sketch, "E63.8.0.26", {"start": v(103.68, 22) * mm, "mid": v(102.38, 20.17) * mm, "end": v(103.66, 18.33) * mm});
            skPoint(sketch, "E63.8.0.27", {"position": v(99.11, 18.23) * mm});
            skPoint(sketch, "E63.8.0.31", {"position": v(104.09, 18.23) * mm});
            skPoint(sketch, "E63.8.0.33", {"position": v(99.52, 22) * mm});
            skArc(sketch, "E63.8.0.34", {"start": v(99.52, 22) * mm, "mid": v(100.82, 20.17) * mm, "end": v(99.54, 18.33) * mm});
            skArc(sketch, "E63.8.0.43", {"start": v(104.09, 17.71) * mm, "mid": v(103.97, 18.09) * mm, "end": v(103.66, 18.33) * mm});
            skArc(sketch, "E63.8.0.44", {"start": v(99.11, 17.71) * mm, "mid": v(99.23, 18.09) * mm, "end": v(99.54, 18.33) * mm});
            skArc(sketch, "E63.8.0.48", {"start": v(103.25, 3.46) * mm, "mid": v(102.4, 2.1) * mm, "end": v(103.25, 0.73) * mm});
            skLineSegment(sketch, "E63.8.0.52", {"start": v(103.93, 2.1) * mm, "end": v(101, 2.1) * mm, "construction": true});
            skArc(sketch, "E63.8.0.59", {"start": v(99.95, 3.46) * mm, "mid": v(100.8, 2.1) * mm, "end": v(99.95, 0.73) * mm});
            skLineSegment(sketch, "E63.8.0.61", {"start": v(99.11, 17.71) * mm, "end": v(99.11, 4.82) * mm});
            skArc(sketch, "E63.8.0.73", {"start": v(103.25, 0.73) * mm, "mid": v(103.86, 0.17) * mm, "end": v(104.09, -0.63) * mm});
            skArc(sketch, "E63.8.0.74", {"start": v(103.25, 3.46) * mm, "mid": v(103.86, 4.02) * mm, "end": v(104.09, 4.82) * mm});
            skArc(sketch, "E63.8.0.75", {"start": v(99.95, 0.73) * mm, "mid": v(99.34, 0.17) * mm, "end": v(99.11, -0.63) * mm});
            skArc(sketch, "E63.8.0.76", {"start": v(99.95, 3.46) * mm, "mid": v(99.34, 4.02) * mm, "end": v(99.11, 4.82) * mm});
            skLineSegment(sketch, "E63.8.0.77", {"start": v(104.09, 17.71) * mm, "end": v(104.09, 4.82) * mm});
            skLineSegment(sketch, "E63.8.0.78", {"start": v(104.09, -0.63) * mm, "end": v(104.09, -15.76) * mm});
            skLineSegment(sketch, "E63.8.0.79", {"start": v(99.11, -0.63) * mm, "end": v(99.11, -15.76) * mm});
            skLineSegment(sketch, "E63.8.0.80", {"start": v(99.36, -16.02) * mm, "end": v(103.84, -16.02) * mm});
            skPoint(sketch, "E63.8.0.81", {"position": v(99.11, -16.02) * mm});
            skPoint(sketch, "E63.8.0.82", {"position": v(104.09, -16.02) * mm});
            skArc(sketch, "E63.8.0.93", {"start": v(103.84, -16.02) * mm, "mid": v(104.01, -15.94) * mm, "end": v(104.09, -15.76) * mm});
            skArc(sketch, "E63.8.0.94", {"start": v(99.11, -15.76) * mm, "mid": v(99.19, -15.94) * mm, "end": v(99.36, -16.02) * mm});
            skPoint(sketch, "E63.9.0.1", {"position": v(116.38, 22) * mm});
            skArc(sketch, "E63.9.0.6", {"start": v(111.81, 25.07) * mm, "mid": v(112.1, 24.6) * mm, "end": v(112.2, 24.06) * mm});
            skLineSegment(sketch, "E63.9.0.7", {"start": v(111.81, 26.05) * mm, "end": v(111.81, 25.07) * mm});
            skLineSegment(sketch, "E63.9.0.9", {"start": v(112.22, 22) * mm, "end": v(112.2, 24.06) * mm});
            skArc(sketch, "E63.9.0.11", {"start": v(116.79, 25.07) * mm, "mid": v(116.5, 24.6) * mm, "end": v(116.4, 24.06) * mm});
            skLineSegment(sketch, "E63.9.0.12", {"start": v(116.38, 22) * mm, "end": v(116.4, 24.06) * mm});
            skLineSegment(sketch, "E63.9.0.21", {"start": v(111.81, 26.05) * mm, "end": v(116.79, 26.05) * mm});
            skLineSegment(sketch, "E63.9.0.22", {"start": v(116.79, 26.05) * mm, "end": v(116.79, 25.07) * mm});
            skArc(sketch, "E63.9.0.26", {"start": v(116.38, 22) * mm, "mid": v(115.08, 20.17) * mm, "end": v(116.36, 18.33) * mm});
            skPoint(sketch, "E63.9.0.27", {"position": v(111.81, 18.23) * mm});
            skPoint(sketch, "E63.9.0.31", {"position": v(116.79, 18.23) * mm});
            skPoint(sketch, "E63.9.0.33", {"position": v(112.22, 22) * mm});
            skArc(sketch, "E63.9.0.34", {"start": v(112.22, 22) * mm, "mid": v(113.52, 20.17) * mm, "end": v(112.24, 18.33) * mm});
            skArc(sketch, "E63.9.0.43", {"start": v(116.79, 17.71) * mm, "mid": v(116.67, 18.09) * mm, "end": v(116.36, 18.33) * mm});
            skArc(sketch, "E63.9.0.44", {"start": v(111.81, 17.71) * mm, "mid": v(111.93, 18.09) * mm, "end": v(112.24, 18.33) * mm});
            skArc(sketch, "E63.9.0.48", {"start": v(115.95, 3.46) * mm, "mid": v(115.1, 2.1) * mm, "end": v(115.95, 0.73) * mm});
            skLineSegment(sketch, "E63.9.0.52", {"start": v(116.63, 2.1) * mm, "end": v(113.7, 2.1) * mm, "construction": true});
            skArc(sketch, "E63.9.0.59", {"start": v(112.65, 3.46) * mm, "mid": v(113.5, 2.1) * mm, "end": v(112.65, 0.73) * mm});
            skLineSegment(sketch, "E63.9.0.61", {"start": v(111.81, 17.71) * mm, "end": v(111.81, 4.82) * mm});
            skArc(sketch, "E63.9.0.73", {"start": v(115.95, 0.73) * mm, "mid": v(116.56, 0.17) * mm, "end": v(116.79, -0.63) * mm});
            skArc(sketch, "E63.9.0.74", {"start": v(115.95, 3.46) * mm, "mid": v(116.56, 4.02) * mm, "end": v(116.79, 4.82) * mm});
            skArc(sketch, "E63.9.0.75", {"start": v(112.65, 0.73) * mm, "mid": v(112.04, 0.17) * mm, "end": v(111.81, -0.63) * mm});
            skArc(sketch, "E63.9.0.76", {"start": v(112.65, 3.46) * mm, "mid": v(112.04, 4.02) * mm, "end": v(111.81, 4.82) * mm});
            skLineSegment(sketch, "E63.9.0.77", {"start": v(116.79, 17.71) * mm, "end": v(116.79, 4.82) * mm});
            skLineSegment(sketch, "E63.9.0.78", {"start": v(116.79, -0.63) * mm, "end": v(116.79, -15.76) * mm});
            skLineSegment(sketch, "E63.9.0.79", {"start": v(111.81, -0.63) * mm, "end": v(111.81, -15.76) * mm});
            skLineSegment(sketch, "E63.9.0.80", {"start": v(112.06, -16.02) * mm, "end": v(116.54, -16.02) * mm});
            skPoint(sketch, "E63.9.0.81", {"position": v(111.81, -16.02) * mm});
            skPoint(sketch, "E63.9.0.82", {"position": v(116.79, -16.02) * mm});
            skArc(sketch, "E63.9.0.93", {"start": v(116.54, -16.02) * mm, "mid": v(116.71, -15.94) * mm, "end": v(116.79, -15.76) * mm});
            skArc(sketch, "E63.9.0.94", {"start": v(111.81, -15.76) * mm, "mid": v(111.89, -15.94) * mm, "end": v(112.06, -16.02) * mm});
            skPoint(sketch, "E63.10.0.1", {"position": v(129.08, 22) * mm});
            skArc(sketch, "E63.10.0.6", {"start": v(124.51, 25.07) * mm, "mid": v(124.8, 24.6) * mm, "end": v(124.9, 24.06) * mm});
            skLineSegment(sketch, "E63.10.0.7", {"start": v(124.51, 26.05) * mm, "end": v(124.51, 25.07) * mm});
            skLineSegment(sketch, "E63.10.0.9", {"start": v(124.92, 22) * mm, "end": v(124.9, 24.06) * mm});
            skArc(sketch, "E63.10.0.11", {"start": v(129.49, 25.07) * mm, "mid": v(129.2, 24.6) * mm, "end": v(129.1, 24.06) * mm});
            skLineSegment(sketch, "E63.10.0.12", {"start": v(129.08, 22) * mm, "end": v(129.1, 24.06) * mm});
            skLineSegment(sketch, "E63.10.0.21", {"start": v(124.51, 26.05) * mm, "end": v(129.49, 26.05) * mm});
            skLineSegment(sketch, "E63.10.0.22", {"start": v(129.49, 26.05) * mm, "end": v(129.49, 25.07) * mm});
            skArc(sketch, "E63.10.0.26", {"start": v(129.08, 22) * mm, "mid": v(127.78, 20.17) * mm, "end": v(129.06, 18.33) * mm});
            skPoint(sketch, "E63.10.0.27", {"position": v(124.51, 18.23) * mm});
            skPoint(sketch, "E63.10.0.31", {"position": v(129.49, 18.23) * mm});
            skPoint(sketch, "E63.10.0.33", {"position": v(124.92, 22) * mm});
            skArc(sketch, "E63.10.0.34", {"start": v(124.92, 22) * mm, "mid": v(126.22, 20.17) * mm, "end": v(124.94, 18.33) * mm});
            skArc(sketch, "E63.10.0.43", {"start": v(129.49, 17.71) * mm, "mid": v(129.37, 18.09) * mm, "end": v(129.06, 18.33) * mm});
            skArc(sketch, "E63.10.0.44", {"start": v(124.51, 17.71) * mm, "mid": v(124.63, 18.09) * mm, "end": v(124.94, 18.33) * mm});
            skArc(sketch, "E63.10.0.48", {"start": v(128.65, 3.46) * mm, "mid": v(127.8, 2.1) * mm, "end": v(128.65, 0.73) * mm});
            skLineSegment(sketch, "E63.10.0.52", {"start": v(129.33, 2.1) * mm, "end": v(126.4, 2.1) * mm, "construction": true});
            skArc(sketch, "E63.10.0.59", {"start": v(125.35, 3.46) * mm, "mid": v(126.2, 2.1) * mm, "end": v(125.35, 0.73) * mm});
            skLineSegment(sketch, "E63.10.0.61", {"start": v(124.51, 17.71) * mm, "end": v(124.51, 4.82) * mm});
            skArc(sketch, "E63.10.0.73", {"start": v(128.65, 0.73) * mm, "mid": v(129.26, 0.17) * mm, "end": v(129.49, -0.63) * mm});
            skArc(sketch, "E63.10.0.74", {"start": v(128.65, 3.46) * mm, "mid": v(129.26, 4.02) * mm, "end": v(129.49, 4.82) * mm});
            skArc(sketch, "E63.10.0.75", {"start": v(125.35, 0.73) * mm, "mid": v(124.74, 0.17) * mm, "end": v(124.51, -0.63) * mm});
            skArc(sketch, "E63.10.0.76", {"start": v(125.35, 3.46) * mm, "mid": v(124.74, 4.02) * mm, "end": v(124.51, 4.82) * mm});
            skLineSegment(sketch, "E63.10.0.77", {"start": v(129.49, 17.71) * mm, "end": v(129.49, 4.82) * mm});
            skLineSegment(sketch, "E63.10.0.78", {"start": v(129.49, -0.63) * mm, "end": v(129.49, -15.76) * mm});
            skLineSegment(sketch, "E63.10.0.79", {"start": v(124.51, -0.63) * mm, "end": v(124.51, -15.76) * mm});
            skLineSegment(sketch, "E63.10.0.80", {"start": v(124.76, -16.02) * mm, "end": v(129.24, -16.02) * mm});
            skPoint(sketch, "E63.10.0.81", {"position": v(124.51, -16.02) * mm});
            skPoint(sketch, "E63.10.0.82", {"position": v(129.49, -16.02) * mm});
            skArc(sketch, "E63.10.0.93", {"start": v(129.24, -16.02) * mm, "mid": v(129.41, -15.94) * mm, "end": v(129.49, -15.76) * mm});
            skArc(sketch, "E63.10.0.94", {"start": v(124.51, -15.76) * mm, "mid": v(124.59, -15.94) * mm, "end": v(124.76, -16.02) * mm});
            skLineSegment(sketch, "E63.direction1", {"start": v(2.49, 4.82) * mm, "end": v(15.19, 4.82) * mm, "construction": true});
            skArc(sketch, "E64.MirrorCS", {"start": v(-103.84, -16.02) * mm, "mid": v(-104.01, -15.94) * mm, "end": v(-104.09, -15.76) * mm});
            skArc(sketch, "E65.MirrorCS", {"start": v(-129.24, -16.02) * mm, "mid": v(-129.41, -15.94) * mm, "end": v(-129.49, -15.76) * mm});
            skArc(sketch, "E66.MirrorCS", {"start": v(-10.21, -15.76) * mm, "mid": v(-10.29, -15.94) * mm, "end": v(-10.46, -16.02) * mm});
            skArc(sketch, "E67.MirrorCS", {"start": v(-35.61, -15.76) * mm, "mid": v(-35.69, -15.94) * mm, "end": v(-35.86, -16.02) * mm});
            skArc(sketch, "E68.MirrorCS", {"start": v(-61.01, -15.76) * mm, "mid": v(-61.09, -15.94) * mm, "end": v(-61.26, -16.02) * mm});
            skArc(sketch, "E69.MirrorCS", {"start": v(-86.41, -15.76) * mm, "mid": v(-86.49, -15.94) * mm, "end": v(-86.66, -16.02) * mm});
            skArc(sketch, "E70.MirrorCS", {"start": v(-27.64, -16.02) * mm, "mid": v(-27.81, -15.94) * mm, "end": v(-27.89, -15.76) * mm});
            skArc(sketch, "E71.MirrorCS", {"start": v(-53.04, -16.02) * mm, "mid": v(-53.21, -15.94) * mm, "end": v(-53.29, -15.76) * mm});
            skArc(sketch, "E72.MirrorCS", {"start": v(-78.44, -16.02) * mm, "mid": v(-78.61, -15.94) * mm, "end": v(-78.69, -15.76) * mm});
            skArc(sketch, "E73.MirrorCS", {"start": v(-73.71, -15.76) * mm, "mid": v(-73.79, -15.94) * mm, "end": v(-73.96, -16.02) * mm});
            skArc(sketch, "E74.MirrorCS", {"start": v(-14.94, -16.02) * mm, "mid": v(-15.11, -15.94) * mm, "end": v(-15.19, -15.76) * mm});
            skArc(sketch, "E75.MirrorCS", {"start": v(-99.11, -15.76) * mm, "mid": v(-99.19, -15.94) * mm, "end": v(-99.36, -16.02) * mm});
            skArc(sketch, "E76.MirrorCS", {"start": v(-124.51, -15.76) * mm, "mid": v(-124.59, -15.94) * mm, "end": v(-124.76, -16.02) * mm});
            skArc(sketch, "E77.MirrorCS", {"start": v(-40.34, -16.02) * mm, "mid": v(-40.51, -15.94) * mm, "end": v(-40.59, -15.76) * mm});
            skArc(sketch, "E78.MirrorCS", {"start": v(-65.74, -16.02) * mm, "mid": v(-65.91, -15.94) * mm, "end": v(-65.99, -15.76) * mm});
            skArc(sketch, "E79.MirrorCS", {"start": v(-91.14, -16.02) * mm, "mid": v(-91.31, -15.94) * mm, "end": v(-91.39, -15.76) * mm});
            skArc(sketch, "E80.MirrorCS", {"start": v(-116.54, -16.02) * mm, "mid": v(-116.71, -15.94) * mm, "end": v(-116.79, -15.76) * mm});
            skArc(sketch, "E81.MirrorCS", {"start": v(-111.81, -15.76) * mm, "mid": v(-111.89, -15.94) * mm, "end": v(-112.06, -16.02) * mm});
            skArc(sketch, "E82.MirrorCS", {"start": v(-22.91, -15.76) * mm, "mid": v(-22.99, -15.94) * mm, "end": v(-23.16, -16.02) * mm});
            skArc(sketch, "E83.MirrorCS", {"start": v(-48.31, -15.76) * mm, "mid": v(-48.39, -15.94) * mm, "end": v(-48.56, -16.02) * mm});
            skLineSegment(sketch, "E84.MirrorCS", {"start": v(-104.09, 26.05) * mm, "end": v(-104.09, 25.07) * mm});
            skArc(sketch, "E85.MirrorCS", {"start": v(-48.31, 17.71) * mm, "mid": v(-48.43, 18.09) * mm, "end": v(-48.74, 18.33) * mm});
            skArc(sketch, "E86.MirrorCS", {"start": v(-78.69, 17.71) * mm, "mid": v(-78.57, 18.09) * mm, "end": v(-78.26, 18.33) * mm});
            skArc(sketch, "E87.MirrorCS", {"start": v(-86.41, 25.07) * mm, "mid": v(-86.7, 24.6) * mm, "end": v(-86.8, 24.06) * mm});
            skArc(sketch, "E88.MirrorCS", {"start": v(-73.71, 17.71) * mm, "mid": v(-73.83, 18.09) * mm, "end": v(-74.14, 18.33) * mm});
            skLineSegment(sketch, "E89.MirrorCS", {"start": v(-86.41, 26.05) * mm, "end": v(-86.41, 25.07) * mm});
            skArc(sketch, "E90.MirrorCS", {"start": v(-104.09, 17.71) * mm, "mid": v(-103.97, 18.09) * mm, "end": v(-103.66, 18.33) * mm});
            skArc(sketch, "E91.MirrorCS", {"start": v(-99.11, 17.71) * mm, "mid": v(-99.23, 18.09) * mm, "end": v(-99.54, 18.33) * mm});
            skArc(sketch, "E92.MirrorCS", {"start": v(-15.19, 17.71) * mm, "mid": v(-15.07, 18.09) * mm, "end": v(-14.76, 18.33) * mm});
            skArc(sketch, "E93.MirrorCS", {"start": v(-129.49, 17.71) * mm, "mid": v(-129.37, 18.09) * mm, "end": v(-129.06, 18.33) * mm});
            skArc(sketch, "E94.MirrorCS", {"start": v(-10.21, 17.71) * mm, "mid": v(-10.33, 18.09) * mm, "end": v(-10.64, 18.33) * mm});
            skArc(sketch, "E95.MirrorCS", {"start": v(-40.59, 17.71) * mm, "mid": v(-40.47, 18.09) * mm, "end": v(-40.16, 18.33) * mm});
            skArc(sketch, "E96.MirrorCS", {"start": v(-124.51, 17.71) * mm, "mid": v(-124.63, 18.09) * mm, "end": v(-124.94, 18.33) * mm});
            skArc(sketch, "E97.MirrorCS", {"start": v(-35.61, 17.71) * mm, "mid": v(-35.73, 18.09) * mm, "end": v(-36.04, 18.33) * mm});
            skArc(sketch, "E98.MirrorCS", {"start": v(-65.99, 17.71) * mm, "mid": v(-65.87, 18.09) * mm, "end": v(-65.56, 18.33) * mm});
            skArc(sketch, "E99.MirrorCS", {"start": v(-61.01, 17.71) * mm, "mid": v(-61.13, 18.09) * mm, "end": v(-61.44, 18.33) * mm});
            skArc(sketch, "E100.MirrorCS", {"start": v(-99.11, 25.07) * mm, "mid": v(-99.4, 24.6) * mm, "end": v(-99.5, 24.06) * mm});
            skArc(sketch, "E101.MirrorCS", {"start": v(-91.39, 17.71) * mm, "mid": v(-91.27, 18.09) * mm, "end": v(-90.96, 18.33) * mm});
            skLineSegment(sketch, "E102.MirrorCS", {"start": v(-99.11, 26.05) * mm, "end": v(-99.11, 25.07) * mm});
            skArc(sketch, "E103.MirrorCS", {"start": v(-86.41, 17.71) * mm, "mid": v(-86.53, 18.09) * mm, "end": v(-86.84, 18.33) * mm});
            skArc(sketch, "E104.MirrorCS", {"start": v(-116.79, 17.71) * mm, "mid": v(-116.67, 18.09) * mm, "end": v(-116.36, 18.33) * mm});
            skArc(sketch, "E105.MirrorCS", {"start": v(-27.89, 17.71) * mm, "mid": v(-27.77, 18.09) * mm, "end": v(-27.46, 18.33) * mm});
            skArc(sketch, "E106.MirrorCS", {"start": v(-104.09, 25.07) * mm, "mid": v(-103.8, 24.6) * mm, "end": v(-103.7, 24.06) * mm});
            skArc(sketch, "E107.MirrorCS", {"start": v(-111.81, 17.71) * mm, "mid": v(-111.93, 18.09) * mm, "end": v(-112.24, 18.33) * mm});
            skArc(sketch, "E108.MirrorCS", {"start": v(-22.91, 17.71) * mm, "mid": v(-23.03, 18.09) * mm, "end": v(-23.34, 18.33) * mm});
            skArc(sketch, "E109.MirrorCS", {"start": v(-53.29, 17.71) * mm, "mid": v(-53.17, 18.09) * mm, "end": v(-52.86, 18.33) * mm});
            skArc(sketch, "E110.MirrorCS", {"start": v(-61.85, 0.73) * mm, "mid": v(-61.24, 0.17) * mm, "end": v(-61.01, -0.63) * mm});
            skLineSegment(sketch, "E111.MirrorCS", {"start": v(-61.01, 26.05) * mm, "end": v(-61.01, 25.07) * mm});
            skArc(sketch, "E112.MirrorCS", {"start": v(-90.55, 0.73) * mm, "mid": v(-91.16, 0.17) * mm, "end": v(-91.39, -0.63) * mm});
            skLineSegment(sketch, "E113.MirrorCS", {"start": v(-15.19, 26.05) * mm, "end": v(-15.19, 25.07) * mm});
            skArc(sketch, "E114.MirrorCS", {"start": v(-40.59, 25.07) * mm, "mid": v(-40.3, 24.6) * mm, "end": v(-40.2, 24.06) * mm});
            skLineSegment(sketch, "E115.MirrorCS", {"start": v(-40.18, 22) * mm, "end": v(-40.2, 24.06) * mm});
            skLineSegment(sketch, "E116.MirrorCS", {"start": v(-61.42, 22) * mm, "end": v(-61.4, 24.06) * mm});
            skArc(sketch, "E117.MirrorCS", {"start": v(-61.85, 3.46) * mm, "mid": v(-61.24, 4.02) * mm, "end": v(-61.01, 4.82) * mm});
            skArc(sketch, "E118.MirrorCS", {"start": v(-90.55, 3.46) * mm, "mid": v(-91.16, 4.02) * mm, "end": v(-91.39, 4.82) * mm});
            skArc(sketch, "E119.MirrorCS", {"start": v(-65.99, 25.07) * mm, "mid": v(-65.7, 24.6) * mm, "end": v(-65.6, 24.06) * mm});
            skArc(sketch, "E120.MirrorCS", {"start": v(-87.25, 0.73) * mm, "mid": v(-86.64, 0.17) * mm, "end": v(-86.41, -0.63) * mm});
            skLineSegment(sketch, "E121.MirrorCS", {"start": v(-129.49, 26.05) * mm, "end": v(-129.49, 25.07) * mm});
            skArc(sketch, "E122.MirrorCS", {"start": v(-115.95, 0.73) * mm, "mid": v(-116.56, 0.17) * mm, "end": v(-116.79, -0.63) * mm});
            skLineSegment(sketch, "E123.MirrorCS", {"start": v(-65.58, 22) * mm, "end": v(-65.6, 24.06) * mm});
            skArc(sketch, "E124.MirrorCS", {"start": v(-111.81, 25.07) * mm, "mid": v(-112.1, 24.6) * mm, "end": v(-112.2, 24.06) * mm});
            skArc(sketch, "E125.MirrorCS", {"start": v(-87.25, 3.46) * mm, "mid": v(-86.64, 4.02) * mm, "end": v(-86.41, 4.82) * mm});
            skLineSegment(sketch, "E126.MirrorCS", {"start": v(-86.82, 22) * mm, "end": v(-86.8, 24.06) * mm});
            skArc(sketch, "E127.MirrorCS", {"start": v(-115.95, 3.46) * mm, "mid": v(-116.56, 4.02) * mm, "end": v(-116.79, 4.82) * mm});
            skLineSegment(sketch, "E128.MirrorCS", {"start": v(-40.59, 26.05) * mm, "end": v(-40.59, 25.07) * mm});
            skArc(sketch, "E129.MirrorCS", {"start": v(-27.05, 0.73) * mm, "mid": v(-27.66, 0.17) * mm, "end": v(-27.89, -0.63) * mm});
            skLineSegment(sketch, "E130.MirrorCS", {"start": v(-111.81, 26.05) * mm, "end": v(-111.81, 25.07) * mm});
            skArc(sketch, "E131.MirrorCS", {"start": v(-91.39, 25.07) * mm, "mid": v(-91.1, 24.6) * mm, "end": v(-91, 24.06) * mm});
            skArc(sketch, "E132.MirrorCS", {"start": v(-112.65, 0.73) * mm, "mid": v(-112.04, 0.17) * mm, "end": v(-111.81, -0.63) * mm});
            skArc(sketch, "E133.MirrorCS", {"start": v(-27.05, 3.46) * mm, "mid": v(-27.66, 4.02) * mm, "end": v(-27.89, 4.82) * mm});
            skArc(sketch, "E134.MirrorCS", {"start": v(-22.91, 25.07) * mm, "mid": v(-23.2, 24.6) * mm, "end": v(-23.3, 24.06) * mm});
            skArc(sketch, "E135.MirrorCS", {"start": v(-112.65, 3.46) * mm, "mid": v(-112.04, 4.02) * mm, "end": v(-111.81, 4.82) * mm});
            skArc(sketch, "E136.MirrorCS", {"start": v(-23.75, 0.73) * mm, "mid": v(-23.14, 0.17) * mm, "end": v(-22.91, -0.63) * mm});
            skLineSegment(sketch, "E137.MirrorCS", {"start": v(-22.91, 26.05) * mm, "end": v(-22.91, 25.07) * mm});
            skLineSegment(sketch, "E138.MirrorCS", {"start": v(-65.99, 26.05) * mm, "end": v(-65.99, 25.07) * mm});
            skArc(sketch, "E139.MirrorCS", {"start": v(-52.45, 0.73) * mm, "mid": v(-53.06, 0.17) * mm, "end": v(-53.29, -0.63) * mm});
            skLineSegment(sketch, "E140.MirrorCS", {"start": v(-129.08, 22) * mm, "end": v(-129.1, 24.06) * mm});
            skLineSegment(sketch, "E141.MirrorCS", {"start": v(-112.22, 22) * mm, "end": v(-112.2, 24.06) * mm});
            skLineSegment(sketch, "E142.MirrorCS", {"start": v(-90.98, 22) * mm, "end": v(-91, 24.06) * mm});
            skArc(sketch, "E143.MirrorCS", {"start": v(-23.75, 3.46) * mm, "mid": v(-23.14, 4.02) * mm, "end": v(-22.91, 4.82) * mm});
            skArc(sketch, "E144.MirrorCS", {"start": v(-48.31, 25.07) * mm, "mid": v(-48.6, 24.6) * mm, "end": v(-48.7, 24.06) * mm});
            skLineSegment(sketch, "E145.MirrorCS", {"start": v(-23.32, 22) * mm, "end": v(-23.3, 24.06) * mm});
            skArc(sketch, "E146.MirrorCS", {"start": v(-52.45, 3.46) * mm, "mid": v(-53.06, 4.02) * mm, "end": v(-53.29, 4.82) * mm});
            skArc(sketch, "E147.MirrorCS", {"start": v(-116.79, 25.07) * mm, "mid": v(-116.5, 24.6) * mm, "end": v(-116.4, 24.06) * mm});
            skLineSegment(sketch, "E148.MirrorCS", {"start": v(-48.31, 26.05) * mm, "end": v(-48.31, 25.07) * mm});
            skArc(sketch, "E149.MirrorCS", {"start": v(-27.89, 25.07) * mm, "mid": v(-27.6, 24.6) * mm, "end": v(-27.5, 24.06) * mm});
            skArc(sketch, "E150.MirrorCS", {"start": v(-77.85, 0.73) * mm, "mid": v(-78.46, 0.17) * mm, "end": v(-78.69, -0.63) * mm});
            skArc(sketch, "E151.MirrorCS", {"start": v(-49.15, 0.73) * mm, "mid": v(-48.54, 0.17) * mm, "end": v(-48.31, -0.63) * mm});
            skLineSegment(sketch, "E152.MirrorCS", {"start": v(-116.38, 22) * mm, "end": v(-116.4, 24.06) * mm});
            skLineSegment(sketch, "E153.MirrorCS", {"start": v(-91.39, 26.05) * mm, "end": v(-91.39, 25.07) * mm});
            skLineSegment(sketch, "E154.MirrorCS", {"start": v(-48.72, 22) * mm, "end": v(-48.7, 24.06) * mm});
            skLineSegment(sketch, "E155.MirrorCS", {"start": v(-27.48, 22) * mm, "end": v(-27.5, 24.06) * mm});
            skArc(sketch, "E156.MirrorCS", {"start": v(-77.85, 3.46) * mm, "mid": v(-78.46, 4.02) * mm, "end": v(-78.69, 4.82) * mm});
            skArc(sketch, "E157.MirrorCS", {"start": v(-73.71, 25.07) * mm, "mid": v(-74, 24.6) * mm, "end": v(-74.1, 24.06) * mm});
            skArc(sketch, "E158.MirrorCS", {"start": v(-49.15, 3.46) * mm, "mid": v(-48.54, 4.02) * mm, "end": v(-48.31, 4.82) * mm});
            skArc(sketch, "E159.MirrorCS", {"start": v(-53.29, 25.07) * mm, "mid": v(-53, 24.6) * mm, "end": v(-52.9, 24.06) * mm});
            skLineSegment(sketch, "E160.MirrorCS", {"start": v(-73.71, 26.05) * mm, "end": v(-73.71, 25.07) * mm});
            skArc(sketch, "E161.MirrorCS", {"start": v(-74.55, 0.73) * mm, "mid": v(-73.94, 0.17) * mm, "end": v(-73.71, -0.63) * mm});
            skLineSegment(sketch, "E162.MirrorCS", {"start": v(-116.79, 26.05) * mm, "end": v(-116.79, 25.07) * mm});
            skArc(sketch, "E163.MirrorCS", {"start": v(-103.25, 0.73) * mm, "mid": v(-103.86, 0.17) * mm, "end": v(-104.09, -0.63) * mm});
            skLineSegment(sketch, "E164.MirrorCS", {"start": v(-27.89, 26.05) * mm, "end": v(-27.89, 25.07) * mm});
            skArc(sketch, "E165.MirrorCS", {"start": v(-14.35, 0.73) * mm, "mid": v(-14.96, 0.17) * mm, "end": v(-15.19, -0.63) * mm});
            skLineSegment(sketch, "E166.MirrorCS", {"start": v(-52.88, 22) * mm, "end": v(-52.9, 24.06) * mm});
            skArc(sketch, "E167.MirrorCS", {"start": v(-74.55, 3.46) * mm, "mid": v(-73.94, 4.02) * mm, "end": v(-73.71, 4.82) * mm});
            skLineSegment(sketch, "E168.MirrorCS", {"start": v(-74.12, 22) * mm, "end": v(-74.1, 24.06) * mm});
            skArc(sketch, "E169.MirrorCS", {"start": v(-103.25, 3.46) * mm, "mid": v(-103.86, 4.02) * mm, "end": v(-104.09, 4.82) * mm});
            skArc(sketch, "E170.MirrorCS", {"start": v(-14.35, 3.46) * mm, "mid": v(-14.96, 4.02) * mm, "end": v(-15.19, 4.82) * mm});
            skArc(sketch, "E171.MirrorCS", {"start": v(-10.21, 25.07) * mm, "mid": v(-10.5, 24.6) * mm, "end": v(-10.6, 24.06) * mm});
            skArc(sketch, "E172.MirrorCS", {"start": v(-78.69, 25.07) * mm, "mid": v(-78.4, 24.6) * mm, "end": v(-78.3, 24.06) * mm});
            skArc(sketch, "E173.MirrorCS", {"start": v(-128.65, 0.73) * mm, "mid": v(-129.26, 0.17) * mm, "end": v(-129.49, -0.63) * mm});
            skArc(sketch, "E174.MirrorCS", {"start": v(-99.95, 0.73) * mm, "mid": v(-99.34, 0.17) * mm, "end": v(-99.11, -0.63) * mm});
            skArc(sketch, "E175.MirrorCS", {"start": v(-11.05, 0.73) * mm, "mid": v(-10.44, 0.17) * mm, "end": v(-10.21, -0.63) * mm});
            skLineSegment(sketch, "E176.MirrorCS", {"start": v(-10.21, 26.05) * mm, "end": v(-10.21, 25.07) * mm});
            skLineSegment(sketch, "E177.MirrorCS", {"start": v(-53.29, 26.05) * mm, "end": v(-53.29, 25.07) * mm});
            skArc(sketch, "E178.MirrorCS", {"start": v(-39.75, 0.73) * mm, "mid": v(-40.36, 0.17) * mm, "end": v(-40.59, -0.63) * mm});
            skLineSegment(sketch, "E179.MirrorCS", {"start": v(-99.52, 22) * mm, "end": v(-99.5, 24.06) * mm});
            skArc(sketch, "E180.MirrorCS", {"start": v(-128.65, 3.46) * mm, "mid": v(-129.26, 4.02) * mm, "end": v(-129.49, 4.82) * mm});
            skLineSegment(sketch, "E181.MirrorCS", {"start": v(-78.28, 22) * mm, "end": v(-78.3, 24.06) * mm});
            skArc(sketch, "E182.MirrorCS", {"start": v(-124.51, 25.07) * mm, "mid": v(-124.8, 24.6) * mm, "end": v(-124.9, 24.06) * mm});
            skArc(sketch, "E183.MirrorCS", {"start": v(-99.95, 3.46) * mm, "mid": v(-99.34, 4.02) * mm, "end": v(-99.11, 4.82) * mm});
            skArc(sketch, "E184.MirrorCS", {"start": v(-35.61, 25.07) * mm, "mid": v(-35.9, 24.6) * mm, "end": v(-36, 24.06) * mm});
            skArc(sketch, "E185.MirrorCS", {"start": v(-11.05, 3.46) * mm, "mid": v(-10.44, 4.02) * mm, "end": v(-10.21, 4.82) * mm});
            skLineSegment(sketch, "E186.MirrorCS", {"start": v(-10.62, 22) * mm, "end": v(-10.6, 24.06) * mm});
            skArc(sketch, "E187.MirrorCS", {"start": v(-39.75, 3.46) * mm, "mid": v(-40.36, 4.02) * mm, "end": v(-40.59, 4.82) * mm});
            skLineSegment(sketch, "E188.MirrorCS", {"start": v(-124.51, 26.05) * mm, "end": v(-124.51, 25.07) * mm});
            skArc(sketch, "E189.MirrorCS", {"start": v(-125.35, 0.73) * mm, "mid": v(-124.74, 0.17) * mm, "end": v(-124.51, -0.63) * mm});
            skLineSegment(sketch, "E190.MirrorCS", {"start": v(-35.61, 26.05) * mm, "end": v(-35.61, 25.07) * mm});
            skArc(sketch, "E191.MirrorCS", {"start": v(-65.15, 0.73) * mm, "mid": v(-65.76, 0.17) * mm, "end": v(-65.99, -0.63) * mm});
            skArc(sketch, "E192.MirrorCS", {"start": v(-15.19, 25.07) * mm, "mid": v(-14.9, 24.6) * mm, "end": v(-14.8, 24.06) * mm});
            skArc(sketch, "E193.MirrorCS", {"start": v(-36.45, 0.73) * mm, "mid": v(-35.84, 0.17) * mm, "end": v(-35.61, -0.63) * mm});
            skLineSegment(sketch, "E194.MirrorCS", {"start": v(-103.68, 22) * mm, "end": v(-103.7, 24.06) * mm});
            skLineSegment(sketch, "E195.MirrorCS", {"start": v(-78.69, 26.05) * mm, "end": v(-78.69, 25.07) * mm});
            skLineSegment(sketch, "E196.MirrorCS", {"start": v(-124.92, 22) * mm, "end": v(-124.9, 24.06) * mm});
            skArc(sketch, "E197.MirrorCS", {"start": v(-125.35, 3.46) * mm, "mid": v(-124.74, 4.02) * mm, "end": v(-124.51, 4.82) * mm});
            skArc(sketch, "E198.MirrorCS", {"start": v(-36.45, 3.46) * mm, "mid": v(-35.84, 4.02) * mm, "end": v(-35.61, 4.82) * mm});
            skLineSegment(sketch, "E199.MirrorCS", {"start": v(-14.78, 22) * mm, "end": v(-14.8, 24.06) * mm});
            skLineSegment(sketch, "E200.MirrorCS", {"start": v(-36.02, 22) * mm, "end": v(-36, 24.06) * mm});
            skArc(sketch, "E201.MirrorCS", {"start": v(-65.15, 3.46) * mm, "mid": v(-65.76, 4.02) * mm, "end": v(-65.99, 4.82) * mm});
            skArc(sketch, "E202.MirrorCS", {"start": v(-61.01, 25.07) * mm, "mid": v(-61.3, 24.6) * mm, "end": v(-61.4, 24.06) * mm});
            skArc(sketch, "E203.MirrorCS", {"start": v(-129.49, 25.07) * mm, "mid": v(-129.2, 24.6) * mm, "end": v(-129.1, 24.06) * mm});
            skLineSegment(sketch, "E204.MirrorCS", {"start": v(-27.73, 2.1) * mm, "end": v(-24.8, 2.1) * mm});
            skArc(sketch, "E205.MirrorCS", {"start": v(-23.75, 3.46) * mm, "mid": v(-24.6, 2.1) * mm, "end": v(-23.75, 0.73) * mm});
            skLineSegment(sketch, "E206.MirrorCS", {"start": v(-53.13, 2.1) * mm, "end": v(-50.2, 2.1) * mm});
            skArc(sketch, "E207.MirrorCS", {"start": v(-49.15, 3.46) * mm, "mid": v(-50, 2.1) * mm, "end": v(-49.15, 0.73) * mm});
            skLineSegment(sketch, "E208.MirrorCS", {"start": v(-78.53, 2.1) * mm, "end": v(-75.6, 2.1) * mm});
            skArc(sketch, "E209.MirrorCS", {"start": v(-74.55, 3.46) * mm, "mid": v(-75.4, 2.1) * mm, "end": v(-74.55, 0.73) * mm});
            skLineSegment(sketch, "E210.MirrorCS", {"start": v(-103.93, 2.1) * mm, "end": v(-101, 2.1) * mm});
            skLineSegment(sketch, "E211.MirrorCS", {"start": v(-15.03, 2.1) * mm, "end": v(-12.1, 2.1) * mm});
            skArc(sketch, "E212.MirrorCS", {"start": v(-99.95, 3.46) * mm, "mid": v(-100.8, 2.1) * mm, "end": v(-99.95, 0.73) * mm});
            skArc(sketch, "E213.MirrorCS", {"start": v(-11.05, 3.46) * mm, "mid": v(-11.9, 2.1) * mm, "end": v(-11.05, 0.73) * mm});
            skLineSegment(sketch, "E214.MirrorCS", {"start": v(-129.33, 2.1) * mm, "end": v(-126.4, 2.1) * mm});
            skLineSegment(sketch, "E215.MirrorCS", {"start": v(-40.43, 2.1) * mm, "end": v(-37.5, 2.1) * mm});
            skArc(sketch, "E216.MirrorCS", {"start": v(-125.35, 3.46) * mm, "mid": v(-126.2, 2.1) * mm, "end": v(-125.35, 0.73) * mm});
            skArc(sketch, "E217.MirrorCS", {"start": v(-112.65, 3.46) * mm, "mid": v(-113.5, 2.1) * mm, "end": v(-112.65, 0.73) * mm});
            skArc(sketch, "E218.MirrorCS", {"start": v(-36.45, 3.46) * mm, "mid": v(-37.3, 2.1) * mm, "end": v(-36.45, 0.73) * mm});
            skLineSegment(sketch, "E219.MirrorCS", {"start": v(-65.83, 2.1) * mm, "end": v(-62.9, 2.1) * mm});
            skArc(sketch, "E220.MirrorCS", {"start": v(-61.85, 3.46) * mm, "mid": v(-62.7, 2.1) * mm, "end": v(-61.85, 0.73) * mm});
            skLineSegment(sketch, "E221.MirrorCS", {"start": v(-116.63, 2.1) * mm, "end": v(-113.7, 2.1) * mm});
            skLineSegment(sketch, "E222.MirrorCS", {"start": v(-91.23, 2.1) * mm, "end": v(-88.3, 2.1) * mm});
            skArc(sketch, "E223.MirrorCS", {"start": v(-87.25, 3.46) * mm, "mid": v(-88.1, 2.1) * mm, "end": v(-87.25, 0.73) * mm});
            skLineSegment(sketch, "E224.MirrorCS", {"start": v(-10.21, -0.63) * mm, "end": v(-10.21, -15.76) * mm});
            skArc(sketch, "E225.MirrorCS", {"start": v(-74.12, 22) * mm, "mid": v(-75.42, 20.17) * mm, "end": v(-74.14, 18.33) * mm});
            skLineSegment(sketch, "E226.MirrorCS", {"start": v(-99.36, -16.02) * mm, "end": v(-103.84, -16.02) * mm});
            skLineSegment(sketch, "E227.MirrorCS", {"start": v(-40.59, -0.63) * mm, "end": v(-40.59, -15.76) * mm});
            skLineSegment(sketch, "E228.MirrorCS", {"start": v(-10.21, 26.05) * mm, "end": v(-15.19, 26.05) * mm});
            skLineSegment(sketch, "E229.MirrorCS", {"start": v(-40.59, 17.71) * mm, "end": v(-40.59, 4.82) * mm});
            skLineSegment(sketch, "E230.MirrorCS", {"start": v(-10.46, -16.02) * mm, "end": v(-14.94, -16.02) * mm});
            skArc(sketch, "E231.MirrorCS", {"start": v(-52.45, 3.46) * mm, "mid": v(-51.6, 2.1) * mm, "end": v(-52.45, 0.73) * mm});
            skArc(sketch, "E232.MirrorCS", {"start": v(-103.68, 22) * mm, "mid": v(-102.38, 20.17) * mm, "end": v(-103.66, 18.33) * mm});
            skLineSegment(sketch, "E233.MirrorCS", {"start": v(-124.51, -0.63) * mm, "end": v(-124.51, -15.76) * mm});
            skLineSegment(sketch, "E234.MirrorCS", {"start": v(-124.51, 26.05) * mm, "end": v(-129.49, 26.05) * mm});
            skLineSegment(sketch, "E235.MirrorCS", {"start": v(-111.81, 17.71) * mm, "end": v(-111.81, 4.82) * mm});
            skLineSegment(sketch, "E236.MirrorCS", {"start": v(-35.61, -0.63) * mm, "end": v(-35.61, -15.76) * mm});
            skLineSegment(sketch, "E237.MirrorCS", {"start": v(-22.91, 17.71) * mm, "end": v(-22.91, 4.82) * mm});
            skLineSegment(sketch, "E238.MirrorCS", {"start": v(-35.61, 26.05) * mm, "end": v(-40.59, 26.05) * mm});
            skLineSegment(sketch, "E239.MirrorCS", {"start": v(-65.99, 17.71) * mm, "end": v(-65.99, 4.82) * mm});
            skArc(sketch, "E240.MirrorCS", {"start": v(-99.52, 22) * mm, "mid": v(-100.82, 20.17) * mm, "end": v(-99.54, 18.33) * mm});
            skPoint(sketch, "E241.MirrorP", {"position": v(-22.91, -16.02) * mm});
            skPoint(sketch, "E242.MirrorP", {"position": v(-10.21, 18.23) * mm});
            skPoint(sketch, "E243.MirrorP", {"position": v(-27.48, 22) * mm});
            skPoint(sketch, "E244.MirrorP", {"position": v(-73.71, -16.02) * mm});
            skPoint(sketch, "E245.MirrorP", {"position": v(-78.28, 22) * mm});
            skLineSegment(sketch, "E246.MirrorCS", {"start": v(-124.76, -16.02) * mm, "end": v(-129.24, -16.02) * mm});
            skPoint(sketch, "E247.MirrorP", {"position": v(-61.01, 18.23) * mm});
            skPoint(sketch, "E248.MirrorP", {"position": v(-111.81, 18.23) * mm});
            skPoint(sketch, "E249.MirrorP", {"position": v(-129.08, 22) * mm});
            skPoint(sketch, "E250.MirrorP", {"position": v(-124.51, -16.02) * mm});
            skArc(sketch, "E251.MirrorCS", {"start": v(-14.78, 22) * mm, "mid": v(-13.48, 20.17) * mm, "end": v(-14.76, 18.33) * mm});
            skArc(sketch, "E252.MirrorCS", {"start": v(-77.85, 3.46) * mm, "mid": v(-77, 2.1) * mm, "end": v(-77.85, 0.73) * mm});
            skLineSegment(sketch, "E253.MirrorCS", {"start": v(-65.99, -0.63) * mm, "end": v(-65.99, -15.76) * mm});
            skPoint(sketch, "E254.MirrorP", {"position": v(-15.19, 18.23) * mm});
            skPoint(sketch, "E255.MirrorP", {"position": v(-27.89, -16.02) * mm});
            skPoint(sketch, "E256.MirrorP", {"position": v(-78.69, -16.02) * mm});
            skArc(sketch, "E257.MirrorCS", {"start": v(-129.08, 22) * mm, "mid": v(-127.78, 20.17) * mm, "end": v(-129.06, 18.33) * mm});
            skPoint(sketch, "E258.MirrorP", {"position": v(-65.99, 18.23) * mm});
            skPoint(sketch, "E259.MirrorP", {"position": v(-129.49, -16.02) * mm});
            skPoint(sketch, "E260.MirrorP", {"position": v(-116.79, 18.23) * mm});
            skArc(sketch, "E261.MirrorCS", {"start": v(-10.62, 22) * mm, "mid": v(-11.92, 20.17) * mm, "end": v(-10.64, 18.33) * mm});
            skLineSegment(sketch, "E262.MirrorCS", {"start": v(-35.86, -16.02) * mm, "end": v(-40.34, -16.02) * mm});
            skPoint(sketch, "E263.MirrorP", {"position": v(-10.62, 22) * mm});
            skLineSegment(sketch, "E264.MirrorCS", {"start": v(-91.39, 17.71) * mm, "end": v(-91.39, 4.82) * mm});
            skPoint(sketch, "E265.MirrorP", {"position": v(-61.42, 22) * mm});
            skArc(sketch, "E266.MirrorCS", {"start": v(-124.92, 22) * mm, "mid": v(-126.22, 20.17) * mm, "end": v(-124.94, 18.33) * mm});
            skPoint(sketch, "E267.MirrorP", {"position": v(-112.22, 22) * mm});
            skArc(sketch, "E268.MirrorCS", {"start": v(-40.18, 22) * mm, "mid": v(-38.88, 20.17) * mm, "end": v(-40.16, 18.33) * mm});
            skLineSegment(sketch, "E269.MirrorCS", {"start": v(-61.01, -0.63) * mm, "end": v(-61.01, -15.76) * mm});
            skLineSegment(sketch, "E270.MirrorCS", {"start": v(-61.01, 26.05) * mm, "end": v(-65.99, 26.05) * mm});
            skLineSegment(sketch, "E271.MirrorCS", {"start": v(-48.31, 17.71) * mm, "end": v(-48.31, 4.82) * mm});
            skArc(sketch, "E272.MirrorCS", {"start": v(-36.02, 22) * mm, "mid": v(-37.32, 20.17) * mm, "end": v(-36.04, 18.33) * mm});
            skLineSegment(sketch, "E273.MirrorCS", {"start": v(-61.26, -16.02) * mm, "end": v(-65.74, -16.02) * mm});
            skLineSegment(sketch, "E274.MirrorCS", {"start": v(-91.39, -0.63) * mm, "end": v(-91.39, -15.76) * mm});
            skArc(sketch, "E275.MirrorCS", {"start": v(-103.25, 3.46) * mm, "mid": v(-102.4, 2.1) * mm, "end": v(-103.25, 0.73) * mm});
            skPoint(sketch, "E276.MirrorP", {"position": v(-124.51, 18.23) * mm});
            skPoint(sketch, "E277.MirrorP", {"position": v(-86.41, -16.02) * mm});
            skArc(sketch, "E278.MirrorCS", {"start": v(-14.35, 3.46) * mm, "mid": v(-13.5, 2.1) * mm, "end": v(-14.35, 0.73) * mm});
            skLineSegment(sketch, "E279.MirrorCS", {"start": v(-73.71, 17.71) * mm, "end": v(-73.71, 4.82) * mm});
            skArc(sketch, "E280.MirrorCS", {"start": v(-65.58, 22) * mm, "mid": v(-64.28, 20.17) * mm, "end": v(-65.56, 18.33) * mm});
            skPoint(sketch, "E281.MirrorP", {"position": v(-35.61, -16.02) * mm});
            skPoint(sketch, "E282.MirrorP", {"position": v(-40.18, 22) * mm});
            skLineSegment(sketch, "E283.MirrorCS", {"start": v(-86.41, -0.63) * mm, "end": v(-86.41, -15.76) * mm});
            skLineSegment(sketch, "E284.MirrorCS", {"start": v(-129.49, -0.63) * mm, "end": v(-129.49, -15.76) * mm});
            skPoint(sketch, "E285.MirrorP", {"position": v(-22.91, 18.23) * mm});
            skLineSegment(sketch, "E286.MirrorCS", {"start": v(-86.41, 26.05) * mm, "end": v(-91.39, 26.05) * mm});
            skPoint(sketch, "E287.MirrorP", {"position": v(-90.98, 22) * mm});
            skPoint(sketch, "E288.MirrorP", {"position": v(-73.71, 18.23) * mm});
            skLineSegment(sketch, "E289.MirrorCS", {"start": v(-116.79, 17.71) * mm, "end": v(-116.79, 4.82) * mm});
            skLineSegment(sketch, "E290.MirrorCS", {"start": v(-27.89, 17.71) * mm, "end": v(-27.89, 4.82) * mm});
            skArc(sketch, "E291.MirrorCS", {"start": v(-61.42, 22) * mm, "mid": v(-62.72, 20.17) * mm, "end": v(-61.44, 18.33) * mm});
            skPoint(sketch, "E292.MirrorP", {"position": v(-40.59, -16.02) * mm});
            skLineSegment(sketch, "E293.MirrorCS", {"start": v(-86.66, -16.02) * mm, "end": v(-91.14, -16.02) * mm});
            skPoint(sketch, "E294.MirrorP", {"position": v(-27.89, 18.23) * mm});
            skPoint(sketch, "E295.MirrorP", {"position": v(-116.79, -16.02) * mm});
            skPoint(sketch, "E296.MirrorP", {"position": v(-78.69, 18.23) * mm});
            skArc(sketch, "E297.MirrorCS", {"start": v(-128.65, 3.46) * mm, "mid": v(-127.8, 2.1) * mm, "end": v(-128.65, 0.73) * mm});
            skLineSegment(sketch, "E298.MirrorCS", {"start": v(-116.79, -0.63) * mm, "end": v(-116.79, -15.76) * mm});
            skPoint(sketch, "E299.MirrorP", {"position": v(-129.49, 18.23) * mm});
            skPoint(sketch, "E300.MirrorP", {"position": v(-91.39, -16.02) * mm});
            skArc(sketch, "E301.MirrorCS", {"start": v(-39.75, 3.46) * mm, "mid": v(-38.9, 2.1) * mm, "end": v(-39.75, 0.73) * mm});
            skLineSegment(sketch, "E302.MirrorCS", {"start": v(-27.89, -0.63) * mm, "end": v(-27.89, -15.76) * mm});
            skLineSegment(sketch, "E303.MirrorCS", {"start": v(-111.81, 26.05) * mm, "end": v(-116.79, 26.05) * mm});
            skLineSegment(sketch, "E304.MirrorCS", {"start": v(-99.11, 17.71) * mm, "end": v(-99.11, 4.82) * mm});
            skPoint(sketch, "E305.MirrorP", {"position": v(-104.09, 18.23) * mm});
            skArc(sketch, "E306.MirrorCS", {"start": v(-90.98, 22) * mm, "mid": v(-89.68, 20.17) * mm, "end": v(-90.96, 18.33) * mm});
            skPoint(sketch, "E307.MirrorP", {"position": v(-48.72, 22) * mm});
            skPoint(sketch, "E308.MirrorP", {"position": v(-23.32, 22) * mm});
            skPoint(sketch, "E309.MirrorP", {"position": v(-74.12, 22) * mm});
            skLineSegment(sketch, "E310.MirrorCS", {"start": v(-111.81, -0.63) * mm, "end": v(-111.81, -15.76) * mm});
            skPoint(sketch, "E311.MirrorP", {"position": v(-124.92, 22) * mm});
            skLineSegment(sketch, "E312.MirrorCS", {"start": v(-22.91, 26.05) * mm, "end": v(-27.89, 26.05) * mm});
            skLineSegment(sketch, "E313.MirrorCS", {"start": v(-22.91, -0.63) * mm, "end": v(-22.91, -15.76) * mm});
            skLineSegment(sketch, "E314.MirrorCS", {"start": v(-10.21, 17.71) * mm, "end": v(-10.21, 4.82) * mm});
            skLineSegment(sketch, "E315.MirrorCS", {"start": v(-53.29, 17.71) * mm, "end": v(-53.29, 4.82) * mm});
            skArc(sketch, "E316.MirrorCS", {"start": v(-86.82, 22) * mm, "mid": v(-88.12, 20.17) * mm, "end": v(-86.84, 18.33) * mm});
            skLineSegment(sketch, "E317.MirrorCS", {"start": v(-112.06, -16.02) * mm, "end": v(-116.54, -16.02) * mm});
            skLineSegment(sketch, "E318.MirrorCS", {"start": v(-23.16, -16.02) * mm, "end": v(-27.64, -16.02) * mm});
            skArc(sketch, "E319.MirrorCS", {"start": v(-65.15, 3.46) * mm, "mid": v(-64.3, 2.1) * mm, "end": v(-65.15, 0.73) * mm});
            skLineSegment(sketch, "E320.MirrorCS", {"start": v(-53.29, -0.63) * mm, "end": v(-53.29, -15.76) * mm});
            skLineSegment(sketch, "E321.MirrorCS", {"start": v(-124.51, 17.71) * mm, "end": v(-124.51, 4.82) * mm});
            skPoint(sketch, "E322.MirrorP", {"position": v(-48.31, -16.02) * mm});
            skArc(sketch, "E323.MirrorCS", {"start": v(-116.38, 22) * mm, "mid": v(-115.08, 20.17) * mm, "end": v(-116.36, 18.33) * mm});
            skPoint(sketch, "E324.MirrorP", {"position": v(-52.88, 22) * mm});
            skPoint(sketch, "E325.MirrorP", {"position": v(-35.61, 18.23) * mm});
            skPoint(sketch, "E326.MirrorP", {"position": v(-99.11, -16.02) * mm});
            skPoint(sketch, "E327.MirrorP", {"position": v(-86.41, 18.23) * mm});
            skPoint(sketch, "E328.MirrorP", {"position": v(-103.68, 22) * mm});
            skArc(sketch, "E329.MirrorCS", {"start": v(-27.48, 22) * mm, "mid": v(-26.18, 20.17) * mm, "end": v(-27.46, 18.33) * mm});
            skLineSegment(sketch, "E330.MirrorCS", {"start": v(-48.31, -0.63) * mm, "end": v(-48.31, -15.76) * mm});
            skLineSegment(sketch, "E331.MirrorCS", {"start": v(-48.31, 26.05) * mm, "end": v(-53.29, 26.05) * mm});
            skLineSegment(sketch, "E332.MirrorCS", {"start": v(-35.61, 17.71) * mm, "end": v(-35.61, 4.82) * mm});
            skPoint(sketch, "E333.MirrorP", {"position": v(-99.52, 22) * mm});
            skLineSegment(sketch, "E334.MirrorCS", {"start": v(-78.69, 17.71) * mm, "end": v(-78.69, 4.82) * mm});
            skPoint(sketch, "E335.MirrorP", {"position": v(-53.29, -16.02) * mm});
            skPoint(sketch, "E336.MirrorP", {"position": v(-104.09, -16.02) * mm});
            skPoint(sketch, "E337.MirrorP", {"position": v(-40.59, 18.23) * mm});
            skArc(sketch, "E338.MirrorCS", {"start": v(-112.22, 22) * mm, "mid": v(-113.52, 20.17) * mm, "end": v(-112.24, 18.33) * mm});
            skPoint(sketch, "E339.MirrorP", {"position": v(-91.39, 18.23) * mm});
            skArc(sketch, "E340.MirrorCS", {"start": v(-23.32, 22) * mm, "mid": v(-24.62, 20.17) * mm, "end": v(-23.34, 18.33) * mm});
            skLineSegment(sketch, "E341.MirrorCS", {"start": v(-48.56, -16.02) * mm, "end": v(-53.04, -16.02) * mm});
            skArc(sketch, "E342.MirrorCS", {"start": v(-90.55, 3.46) * mm, "mid": v(-89.7, 2.1) * mm, "end": v(-90.55, 0.73) * mm});
            skLineSegment(sketch, "E343.MirrorCS", {"start": v(-78.69, -0.63) * mm, "end": v(-78.69, -15.76) * mm});
            skPoint(sketch, "E344.MirrorP", {"position": v(-36.02, 22) * mm});
            skPoint(sketch, "E345.MirrorP", {"position": v(-86.82, 22) * mm});
            skLineSegment(sketch, "E346.MirrorCS", {"start": v(-61.01, 17.71) * mm, "end": v(-61.01, 4.82) * mm});
            skArc(sketch, "E347.MirrorCS", {"start": v(-52.88, 22) * mm, "mid": v(-51.58, 20.17) * mm, "end": v(-52.86, 18.33) * mm});
            skLineSegment(sketch, "E348.MirrorCS", {"start": v(-73.71, -0.63) * mm, "end": v(-73.71, -15.76) * mm});
            skLineSegment(sketch, "E349.MirrorCS", {"start": v(-73.71, 26.05) * mm, "end": v(-78.69, 26.05) * mm});
            skLineSegment(sketch, "E350.MirrorCS", {"start": v(-104.09, 17.71) * mm, "end": v(-104.09, 4.82) * mm});
            skLineSegment(sketch, "E351.MirrorCS", {"start": v(-15.19, 17.71) * mm, "end": v(-15.19, 4.82) * mm});
            skArc(sketch, "E352.MirrorCS", {"start": v(-48.72, 22) * mm, "mid": v(-50.02, 20.17) * mm, "end": v(-48.74, 18.33) * mm});
            skPoint(sketch, "E353.MirrorP", {"position": v(-10.21, -16.02) * mm});
            skLineSegment(sketch, "E354.MirrorCS", {"start": v(-73.96, -16.02) * mm, "end": v(-78.44, -16.02) * mm});
            skPoint(sketch, "E355.MirrorP", {"position": v(-14.78, 22) * mm});
            skPoint(sketch, "E356.MirrorP", {"position": v(-65.58, 22) * mm});
            skPoint(sketch, "E357.MirrorP", {"position": v(-61.01, -16.02) * mm});
            skPoint(sketch, "E358.MirrorP", {"position": v(-48.31, 18.23) * mm});
            skArc(sketch, "E359.MirrorCS", {"start": v(-115.95, 3.46) * mm, "mid": v(-115.1, 2.1) * mm, "end": v(-115.95, 0.73) * mm});
            skPoint(sketch, "E360.MirrorP", {"position": v(-116.38, 22) * mm});
            skLineSegment(sketch, "E361.MirrorCS", {"start": v(-104.09, -0.63) * mm, "end": v(-104.09, -15.76) * mm});
            skPoint(sketch, "E362.MirrorP", {"position": v(-99.11, 18.23) * mm});
            skPoint(sketch, "E363.MirrorP", {"position": v(-111.81, -16.02) * mm});
            skArc(sketch, "E364.MirrorCS", {"start": v(-27.05, 3.46) * mm, "mid": v(-26.2, 2.1) * mm, "end": v(-27.05, 0.73) * mm});
            skLineSegment(sketch, "E365.MirrorCS", {"start": v(-15.19, -0.63) * mm, "end": v(-15.19, -15.76) * mm});
            skArc(sketch, "E366.MirrorCS", {"start": v(-78.28, 22) * mm, "mid": v(-76.98, 20.17) * mm, "end": v(-78.26, 18.33) * mm});
            skLineSegment(sketch, "E367.MirrorCS", {"start": v(-99.11, -0.63) * mm, "end": v(-99.11, -15.76) * mm});
            skLineSegment(sketch, "E368.MirrorCS", {"start": v(-99.11, 26.05) * mm, "end": v(-104.09, 26.05) * mm});
            skLineSegment(sketch, "E369.MirrorCS", {"start": v(-86.41, 17.71) * mm, "end": v(-86.41, 4.82) * mm});
            skPoint(sketch, "E370.MirrorP", {"position": v(-15.19, -16.02) * mm});
            skLineSegment(sketch, "E371.MirrorCS", {"start": v(-129.49, 17.71) * mm, "end": v(-129.49, 4.82) * mm});
            skPoint(sketch, "E372.MirrorP", {"position": v(-65.99, -16.02) * mm});
            skPoint(sketch, "E373.MirrorP", {"position": v(-53.29, 18.23) * mm});
            skSolve(sketch);
        }
        {
            var Q0;
            Q0=qSketchRegion(id+"F2",true);
            extrude(context, id + "F3", {"entities" : qUnion([Q0]), "operationType" : NewBodyOperationType.REMOVE, "endBound" : BoundingType.SYMMETRIC, "oppositeDirection" : true, "depth" : 34.92 * mm});
        }
    });
